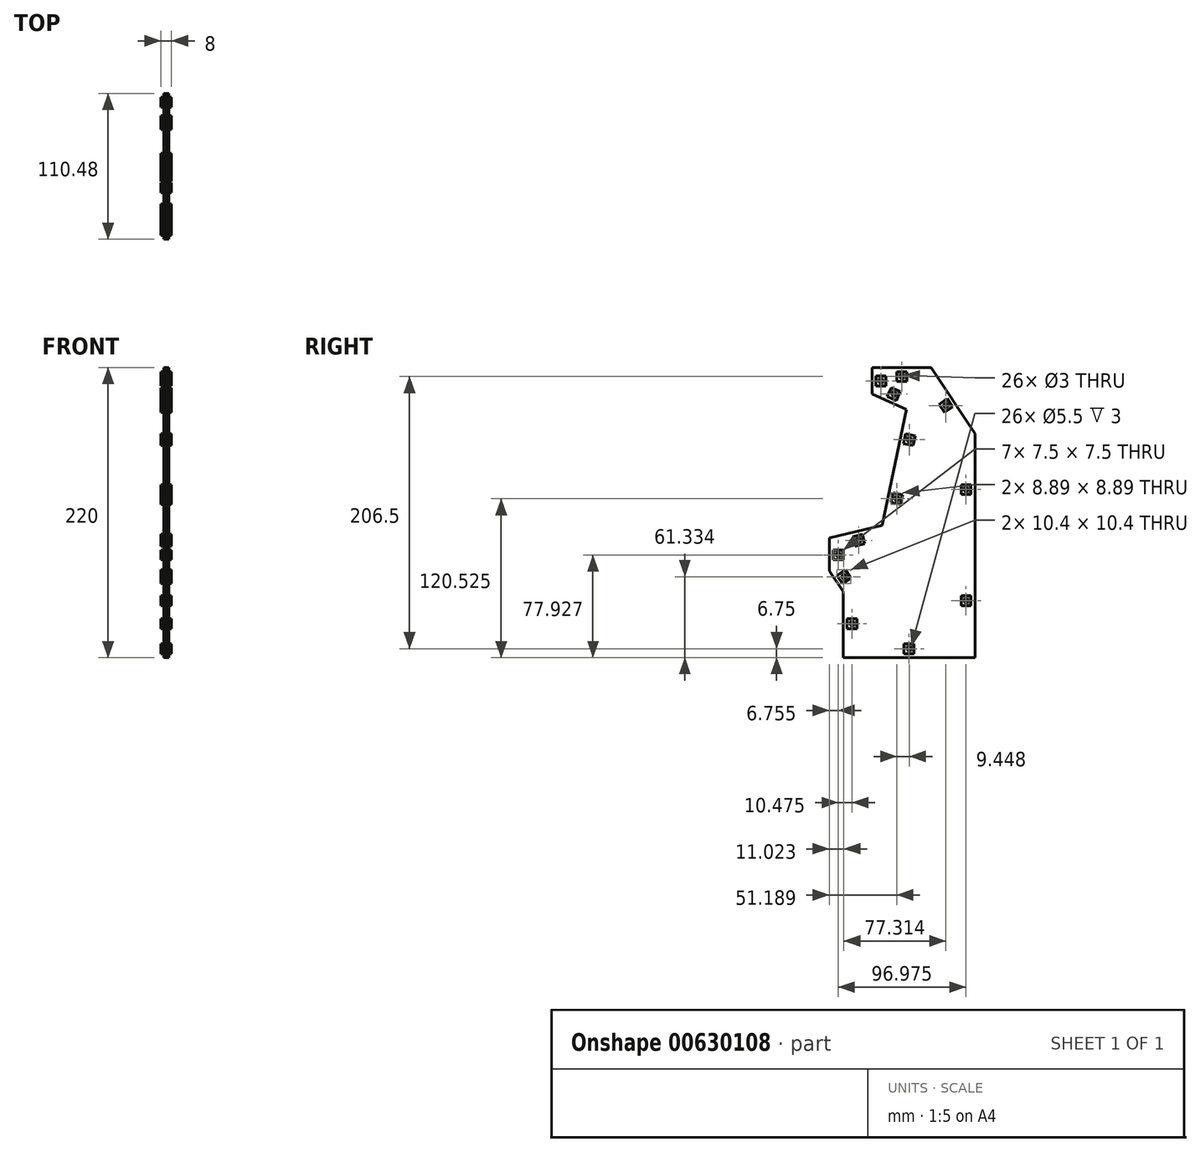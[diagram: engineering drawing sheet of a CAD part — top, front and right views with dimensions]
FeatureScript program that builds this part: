
annotation { "Feature Type Name" : "Feature", "Feature Type Description" : "" }
export const myFeature = defineFeature(function(context is Context, id is Id, definition is map)
    precondition{}
    {
        {
            var Q0;
            Q0=qCreatedBy(makeId("Right.planeOp"),FACE);
            var sketch = newSketch(context, id + "F0", { "sketchPlane" : qUnion([Q0])});
            skLineSegment(sketch, "E0", {"start": v(0, 0) * mm, "end": v(-100, 0) * mm});
            skLineSegment(sketch, "E1", {"start": v(-100, 0) * mm, "end": v(-100, 50) * mm});
            skLineSegment(sketch, "E2", {"start": v(-100, 50) * mm, "end": v(-110.48, 65.67) * mm});
            skLineSegment(sketch, "E3", {"start": v(-110.48, 65.67) * mm, "end": v(-110.48, 90.67) * mm});
            skLineSegment(sketch, "E4", {"start": v(-110.48, 90.67) * mm, "end": v(-70.49, 100.17) * mm});
            skLineSegment(sketch, "E5", {"start": v(-70.49, 100.17) * mm, "end": v(-51.9, 188.23) * mm});
            skLineSegment(sketch, "E6", {"start": v(-51.9, 188.23) * mm, "end": v(-78.17, 200) * mm});
            skLineSegment(sketch, "E7", {"start": v(-78.17, 200) * mm, "end": v(-78.17, 220) * mm});
            skLineSegment(sketch, "E8", {"start": v(-78.17, 220) * mm, "end": v(-33.17, 220) * mm});
            skLineSegment(sketch, "E9", {"start": v(-33.17, 220) * mm, "end": v(0, 170) * mm});
            skLineSegment(sketch, "E10", {"start": v(0, 170) * mm, "end": v(0, 0) * mm});
            skLineSegment(sketch, "E11.0", {"start": v(-109.48, 89.88) * mm, "end": v(-69.64, 99.35) * mm});
            skLineSegment(sketch, "E11.1", {"start": v(-109.48, 65.97) * mm, "end": v(-109.48, 89.88) * mm});
            skLineSegment(sketch, "E11.2", {"start": v(-99, 50.3) * mm, "end": v(-109.48, 65.97) * mm});
            skLineSegment(sketch, "E11.3", {"start": v(-99, 1) * mm, "end": v(-99, 50.3) * mm});
            skLineSegment(sketch, "E11.4", {"start": v(-1, 1) * mm, "end": v(-99, 1) * mm});
            skLineSegment(sketch, "E11.5", {"start": v(-69.64, 99.35) * mm, "end": v(-50.75, 188.81) * mm});
            skLineSegment(sketch, "E11.6", {"start": v(-50.75, 188.81) * mm, "end": v(-77.17, 200.65) * mm});
            skLineSegment(sketch, "E11.7", {"start": v(-77.17, 200.65) * mm, "end": v(-77.17, 219) * mm});
            skLineSegment(sketch, "E11.8", {"start": v(-77.17, 219) * mm, "end": v(-33.7, 219) * mm});
            skLineSegment(sketch, "E11.9", {"start": v(-33.7, 219) * mm, "end": v(-1, 169.7) * mm});
            skLineSegment(sketch, "E11.10", {"start": v(-1, 169.7) * mm, "end": v(-1, 1) * mm});
            skLineSegment(sketch, "E12.0", {"start": v(-75.17, 217) * mm, "end": v(-34.78, 217) * mm});
            skLineSegment(sketch, "E12.1", {"start": v(-75.17, 201.94) * mm, "end": v(-75.17, 217) * mm});
            skLineSegment(sketch, "E12.2", {"start": v(-48.46, 189.98) * mm, "end": v(-75.17, 201.94) * mm});
            skLineSegment(sketch, "E12.3", {"start": v(-67.95, 97.7) * mm, "end": v(-48.46, 189.98) * mm});
            skLineSegment(sketch, "E12.4", {"start": v(-107.48, 88.3) * mm, "end": v(-67.95, 97.7) * mm});
            skLineSegment(sketch, "E12.5", {"start": v(-34.78, 217) * mm, "end": v(-3, 169.1) * mm});
            skLineSegment(sketch, "E12.6", {"start": v(-3, 169.1) * mm, "end": v(-3, 3) * mm});
            skLineSegment(sketch, "E12.7", {"start": v(-3, 3) * mm, "end": v(-97, 3) * mm});
            skLineSegment(sketch, "E12.8", {"start": v(-97, 3) * mm, "end": v(-97, 50.91) * mm});
            skLineSegment(sketch, "E12.9", {"start": v(-97, 50.91) * mm, "end": v(-107.48, 66.58) * mm});
            skLineSegment(sketch, "E12.10", {"start": v(-107.48, 66.58) * mm, "end": v(-107.48, 88.3) * mm});
            skPoint(sketch, "E13", {"position": v(-58.2, 143.84) * mm});
            skPoint(sketch, "E14", {"position": v(-87.71, 93) * mm});
            skSolve(sketch);
        }
        {
            var Q0;
            Q0=makeQuery(id+"F0.imprint","IMPRINT",FACE,{"disambiguationData":[TD([[makeQuery(id+"F0.imprint","IMPRINT",EDGE,{"derivedFrom":sQuery(id+"F0.wireOp",EDGE,"E11.0")}),-1.0]])]});
            var Q1;
            Q1=makeQuery(id+"F0.imprint","IMPRINT",FACE,{"disambiguationData":[TD([[makeQuery(id+"F0.imprint","IMPRINT",EDGE,{"derivedFrom":sQuery(id+"F0.wireOp",EDGE,"E0")}),-1.0]])]});
            var Q2;
            Q2=makeQuery(id+"F0.imprint","IMPRINT",FACE,{"disambiguationData":[TD([[makeQuery(id+"F0.imprint","IMPRINT",EDGE,{"derivedFrom":sQuery(id+"F0.wireOp",EDGE,"E12.0")}),-1.0]])]});
            extrude(context, id + "F1", {"entities" : qUnion([Q0, Q1, Q2]), "depth" : 2 * mm, "offsetDistance" : 25 * mm});
        }
        {
            var Q0;
            Q0=makeQuery(id+"F1.opExtrude","CAP_FACE",FACE,{"disambiguationData":[OSD([sQuery(id+"F0.wireOp",EDGE,"E0"),sQuery(id+"F0.wireOp",EDGE,"E1"),sQuery(id+"F0.wireOp",EDGE,"E2"),sQuery(id+"F0.wireOp",EDGE,"E3"),sQuery(id+"F0.wireOp",EDGE,"E4"),sQuery(id+"F0.wireOp",EDGE,"E5"),sQuery(id+"F0.wireOp",EDGE,"E6"),sQuery(id+"F0.wireOp",EDGE,"E7"),sQuery(id+"F0.wireOp",EDGE,"E8"),sQuery(id+"F0.wireOp",EDGE,"E9"),sQuery(id+"F0.wireOp",EDGE,"E10")])],"isStart":true});
            var sketch = newSketch(context, id + "F2", { "sketchPlane" : qUnion([Q0])});
            skPoint(sketch, "E15", {"position": v(70.49, 100.17) * mm});
            skPoint(sketch, "E16", {"position": v(110.48, 90.67) * mm});
            skPoint(sketch, "E17", {"position": v(89.56, 94.61) * mm});
            skLineSegment(sketch, "E18", {"start": v(89.56, 94.61) * mm, "end": v(88.86, 91.7) * mm});
            skLineSegment(sketch, "E19", {"start": v(86.19, 92.33) * mm, "end": v(88.86, 91.7) * mm});
            skLineSegment(sketch, "E20", {"start": v(88.86, 91.7) * mm, "end": v(91.54, 91.06) * mm});
            skCircle(sketch, "E21", {"center": v(88.23, 89.02) * mm, "radius": 2.75 * mm});
            skLineSegment(sketch, "E22", {"start": v(88.86, 91.7) * mm, "end": v(87.6, 86.34) * mm});
            skLineSegment(sketch, "E23", {"start": v(86.19, 92.33) * mm, "end": v(84.92, 86.98) * mm});
            skLineSegment(sketch, "E24", {"start": v(91.54, 91.06) * mm, "end": v(90.27, 85.7) * mm});
            skLineSegment(sketch, "E25", {"start": v(84.92, 86.98) * mm, "end": v(90.27, 85.7) * mm});
            skLineSegment(sketch, "E26.2", {"start": v(92.74, 91.8) * mm, "end": v(91.01, 84.5) * mm});
            skLineSegment(sketch, "E26.3", {"start": v(83.71, 86.24) * mm, "end": v(91.01, 84.5) * mm});
            skLineSegment(sketch, "E26.4", {"start": v(85.45, 93.53) * mm, "end": v(83.71, 86.24) * mm});
            skCircle(sketch, "E27", {"center": v(88.23, 89.02) * mm, "radius": 1.5 * mm});
            skPoint(sketch, "E28", {"position": v(99, 25.65) * mm});
            skLineSegment(sketch, "E29", {"start": v(99, 25.65) * mm, "end": v(96, 25.65) * mm});
            skLineSegment(sketch, "E30", {"start": v(96, 28.4) * mm, "end": v(96, 25.65) * mm});
            skLineSegment(sketch, "E31", {"start": v(96, 25.65) * mm, "end": v(96, 22.9) * mm});
            skCircle(sketch, "E32", {"center": v(93.25, 25.65) * mm, "radius": 2.75 * mm});
            skLineSegment(sketch, "E33", {"start": v(96, 25.65) * mm, "end": v(90.5, 25.65) * mm});
            skLineSegment(sketch, "E34", {"start": v(96, 28.4) * mm, "end": v(90.5, 28.4) * mm});
            skLineSegment(sketch, "E35", {"start": v(96, 22.9) * mm, "end": v(90.5, 22.9) * mm});
            skLineSegment(sketch, "E36", {"start": v(90.5, 28.4) * mm, "end": v(90.5, 22.9) * mm});
            skLineSegment(sketch, "E37.2", {"start": v(97, 21.9) * mm, "end": v(89.5, 21.9) * mm});
            skLineSegment(sketch, "E37.3", {"start": v(89.5, 29.4) * mm, "end": v(89.5, 21.9) * mm});
            skLineSegment(sketch, "E37.4", {"start": v(97, 29.4) * mm, "end": v(89.5, 29.4) * mm});
            skCircle(sketch, "E38", {"center": v(93.25, 25.65) * mm, "radius": 1.5 * mm});
            skPoint(sketch, "E39", {"position": v(100, 50) * mm});
            skPoint(sketch, "E40", {"position": v(100, 0) * mm});
            skLineSegment(sketch, "E41", {"start": v(97, 21.9) * mm, "end": v(97, 29.4) * mm});
            skPoint(sketch, "E42", {"position": v(50, 0) * mm});
            skLineSegment(sketch, "E43", {"start": v(50, 1) * mm, "end": v(50, 4) * mm});
            skLineSegment(sketch, "E44", {"start": v(52.75, 4) * mm, "end": v(50, 4) * mm});
            skLineSegment(sketch, "E45", {"start": v(50, 4) * mm, "end": v(47.25, 4) * mm});
            skCircle(sketch, "E46", {"center": v(50, 6.75) * mm, "radius": 2.75 * mm});
            skLineSegment(sketch, "E47", {"start": v(50, 4) * mm, "end": v(50, 9.5) * mm});
            skLineSegment(sketch, "E48", {"start": v(52.75, 4) * mm, "end": v(52.75, 9.5) * mm});
            skLineSegment(sketch, "E49", {"start": v(47.25, 4) * mm, "end": v(47.25, 9.5) * mm});
            skLineSegment(sketch, "E50", {"start": v(52.75, 9.5) * mm, "end": v(47.25, 9.5) * mm});
            skLineSegment(sketch, "E51.2", {"start": v(46.25, 3) * mm, "end": v(46.25, 10.5) * mm});
            skLineSegment(sketch, "E51.3", {"start": v(53.75, 10.5) * mm, "end": v(46.25, 10.5) * mm});
            skLineSegment(sketch, "E51.4", {"start": v(53.75, 3) * mm, "end": v(53.75, 10.5) * mm});
            skCircle(sketch, "E52", {"center": v(50, 6.75) * mm, "radius": 1.5 * mm});
            skLineSegment(sketch, "E53", {"start": v(46.25, 3) * mm, "end": v(53.75, 3) * mm});
            skLineSegment(sketch, "E54", {"start": v(85.45, 93.53) * mm, "end": v(92.74, 91.8) * mm});
            skPoint(sketch, "E55", {"position": v(1, 43.17) * mm});
            skLineSegment(sketch, "E56", {"start": v(1, 43.17) * mm, "end": v(4, 43.17) * mm});
            skLineSegment(sketch, "E57", {"start": v(4, 40.42) * mm, "end": v(4, 43.17) * mm});
            skLineSegment(sketch, "E58", {"start": v(4, 43.17) * mm, "end": v(4, 45.92) * mm});
            skCircle(sketch, "E59", {"center": v(6.75, 43.17) * mm, "radius": 2.75 * mm});
            skLineSegment(sketch, "E60", {"start": v(4, 43.17) * mm, "end": v(9.5, 43.17) * mm});
            skLineSegment(sketch, "E61", {"start": v(4, 40.42) * mm, "end": v(9.5, 40.42) * mm});
            skLineSegment(sketch, "E62", {"start": v(4, 45.92) * mm, "end": v(9.5, 45.92) * mm});
            skLineSegment(sketch, "E63", {"start": v(9.5, 40.42) * mm, "end": v(9.5, 45.92) * mm});
            skLineSegment(sketch, "E64.2", {"start": v(3, 46.92) * mm, "end": v(10.5, 46.92) * mm});
            skLineSegment(sketch, "E64.3", {"start": v(10.5, 39.42) * mm, "end": v(10.5, 46.92) * mm});
            skLineSegment(sketch, "E64.4", {"start": v(3, 39.42) * mm, "end": v(10.5, 39.42) * mm});
            skCircle(sketch, "E65", {"center": v(6.75, 43.17) * mm, "radius": 1.5 * mm});
            skLineSegment(sketch, "E66", {"start": v(3, 46.92) * mm, "end": v(3, 39.42) * mm});
            skPoint(sketch, "E67", {"position": v(0, 170) * mm});
            skPoint(sketch, "E68", {"position": v(0, 85) * mm});
            skPoint(sketch, "E69", {"position": v(1, 127.52) * mm});
            skLineSegment(sketch, "E70", {"start": v(1, 127.52) * mm, "end": v(4, 127.52) * mm});
            skLineSegment(sketch, "E71", {"start": v(4, 124.77) * mm, "end": v(4, 127.52) * mm});
            skLineSegment(sketch, "E72", {"start": v(4, 127.52) * mm, "end": v(4, 130.27) * mm});
            skCircle(sketch, "E73", {"center": v(6.75, 127.52) * mm, "radius": 2.75 * mm});
            skLineSegment(sketch, "E74", {"start": v(4, 127.52) * mm, "end": v(9.5, 127.52) * mm});
            skLineSegment(sketch, "E75", {"start": v(4, 124.77) * mm, "end": v(9.5, 124.77) * mm});
            skLineSegment(sketch, "E76", {"start": v(4, 130.27) * mm, "end": v(9.5, 130.27) * mm});
            skLineSegment(sketch, "E77", {"start": v(9.5, 124.77) * mm, "end": v(9.5, 130.27) * mm});
            skLineSegment(sketch, "E78.2", {"start": v(3, 131.27) * mm, "end": v(10.5, 131.27) * mm});
            skLineSegment(sketch, "E78.3", {"start": v(10.5, 123.77) * mm, "end": v(10.5, 131.27) * mm});
            skLineSegment(sketch, "E78.4", {"start": v(3, 123.77) * mm, "end": v(10.5, 123.77) * mm});
            skCircle(sketch, "E79", {"center": v(6.75, 127.52) * mm, "radius": 1.5 * mm});
            skLineSegment(sketch, "E80", {"start": v(3, 131.27) * mm, "end": v(3, 123.77) * mm});
            skPoint(sketch, "E81", {"position": v(17.35, 194.35) * mm});
            skLineSegment(sketch, "E82", {"start": v(17.35, 194.35) * mm, "end": v(19.85, 192.7) * mm});
            skLineSegment(sketch, "E83", {"start": v(18.33, 190.4) * mm, "end": v(19.85, 192.7) * mm});
            skLineSegment(sketch, "E84", {"start": v(19.85, 192.7) * mm, "end": v(21.37, 194.98) * mm});
            skCircle(sketch, "E85", {"center": v(22.14, 191.17) * mm, "radius": 2.75 * mm});
            skLineSegment(sketch, "E86", {"start": v(19.85, 192.7) * mm, "end": v(24.43, 189.65) * mm});
            skLineSegment(sketch, "E87", {"start": v(18.33, 190.4) * mm, "end": v(22.91, 187.36) * mm});
            skLineSegment(sketch, "E88", {"start": v(21.37, 194.98) * mm, "end": v(25.95, 191.94) * mm});
            skLineSegment(sketch, "E89", {"start": v(22.91, 187.36) * mm, "end": v(25.95, 191.94) * mm});
            skLineSegment(sketch, "E90.2", {"start": v(21.1, 196.37) * mm, "end": v(27.34, 192.22) * mm});
            skLineSegment(sketch, "E90.3", {"start": v(23.2, 185.97) * mm, "end": v(27.34, 192.22) * mm});
            skLineSegment(sketch, "E90.4", {"start": v(16.95, 190.12) * mm, "end": v(23.2, 185.97) * mm});
            skCircle(sketch, "E91", {"center": v(22.14, 191.17) * mm, "radius": 1.5 * mm});
            skLineSegment(sketch, "E92", {"start": v(21.1, 196.37) * mm, "end": v(16.95, 190.12) * mm});
            skPoint(sketch, "E93", {"position": v(55.43, 219) * mm});
            skLineSegment(sketch, "E94", {"start": v(55.43, 219) * mm, "end": v(55.43, 216) * mm});
            skLineSegment(sketch, "E95", {"start": v(52.68, 216) * mm, "end": v(55.43, 216) * mm});
            skLineSegment(sketch, "E96", {"start": v(55.43, 216) * mm, "end": v(58.18, 216) * mm});
            skCircle(sketch, "E97", {"center": v(55.43, 213.25) * mm, "radius": 2.75 * mm});
            skLineSegment(sketch, "E98", {"start": v(55.43, 216) * mm, "end": v(55.43, 210.5) * mm});
            skLineSegment(sketch, "E99", {"start": v(52.68, 216) * mm, "end": v(52.68, 210.5) * mm});
            skLineSegment(sketch, "E100", {"start": v(58.18, 216) * mm, "end": v(58.18, 210.5) * mm});
            skLineSegment(sketch, "E101", {"start": v(52.68, 210.5) * mm, "end": v(58.18, 210.5) * mm});
            skLineSegment(sketch, "E102.2", {"start": v(59.18, 217) * mm, "end": v(59.18, 209.5) * mm});
            skLineSegment(sketch, "E102.3", {"start": v(51.68, 209.5) * mm, "end": v(59.18, 209.5) * mm});
            skLineSegment(sketch, "E102.4", {"start": v(51.68, 217) * mm, "end": v(51.68, 209.5) * mm});
            skCircle(sketch, "E103", {"center": v(55.43, 213.25) * mm, "radius": 1.5 * mm});
            skLineSegment(sketch, "E104", {"start": v(59.18, 217) * mm, "end": v(51.68, 217) * mm});
            skPoint(sketch, "E105", {"position": v(63.96, 194.73) * mm});
            skLineSegment(sketch, "E106", {"start": v(63.96, 194.73) * mm, "end": v(62.73, 197.47) * mm});
            skLineSegment(sketch, "E107", {"start": v(65.24, 198.6) * mm, "end": v(62.73, 197.47) * mm});
            skLineSegment(sketch, "E108", {"start": v(62.73, 197.47) * mm, "end": v(60.22, 196.34) * mm});
            skCircle(sketch, "E109", {"center": v(61.6, 199.98) * mm, "radius": 2.75 * mm});
            skLineSegment(sketch, "E110", {"start": v(62.73, 197.47) * mm, "end": v(60.48, 202.49) * mm});
            skLineSegment(sketch, "E111", {"start": v(65.24, 198.6) * mm, "end": v(63, 203.61) * mm});
            skLineSegment(sketch, "E112", {"start": v(60.22, 196.34) * mm, "end": v(57.97, 201.36) * mm});
            skLineSegment(sketch, "E113", {"start": v(63, 203.61) * mm, "end": v(57.97, 201.36) * mm});
            skLineSegment(sketch, "E114.2", {"start": v(59.72, 195.02) * mm, "end": v(56.65, 201.87) * mm});
            skLineSegment(sketch, "E114.3", {"start": v(63.5, 204.93) * mm, "end": v(56.65, 201.87) * mm});
            skLineSegment(sketch, "E114.4", {"start": v(66.56, 198.09) * mm, "end": v(63.5, 204.93) * mm});
            skCircle(sketch, "E115", {"center": v(61.6, 199.98) * mm, "radius": 1.5 * mm});
            skLineSegment(sketch, "E116", {"start": v(59.72, 195.02) * mm, "end": v(66.56, 198.09) * mm});
            skPoint(sketch, "E117", {"position": v(55.47, 166.45) * mm});
            skLineSegment(sketch, "E118", {"start": v(55.47, 166.45) * mm, "end": v(52.53, 165.83) * mm});
            skLineSegment(sketch, "E119", {"start": v(51.97, 168.52) * mm, "end": v(52.53, 165.83) * mm});
            skLineSegment(sketch, "E120", {"start": v(52.53, 165.83) * mm, "end": v(53.1, 163.14) * mm});
            skCircle(sketch, "E121", {"center": v(49.84, 165.26) * mm, "radius": 2.75 * mm});
            skLineSegment(sketch, "E122", {"start": v(52.53, 165.83) * mm, "end": v(47.15, 164.69) * mm});
            skLineSegment(sketch, "E123", {"start": v(51.97, 168.52) * mm, "end": v(46.58, 167.38) * mm});
            skLineSegment(sketch, "E124", {"start": v(53.1, 163.14) * mm, "end": v(47.72, 162) * mm});
            skLineSegment(sketch, "E125", {"start": v(46.58, 167.38) * mm, "end": v(47.72, 162) * mm});
            skLineSegment(sketch, "E126.2", {"start": v(54.29, 162.36) * mm, "end": v(46.95, 160.81) * mm});
            skLineSegment(sketch, "E126.3", {"start": v(45.4, 168.15) * mm, "end": v(46.95, 160.81) * mm});
            skLineSegment(sketch, "E126.4", {"start": v(52.74, 169.7) * mm, "end": v(45.4, 168.15) * mm});
            skCircle(sketch, "E127", {"center": v(49.84, 165.26) * mm, "radius": 1.5 * mm});
            skLineSegment(sketch, "E128", {"start": v(54.29, 162.36) * mm, "end": v(52.74, 169.7) * mm});
            skPoint(sketch, "E129", {"position": v(64.92, 121.71) * mm});
            skLineSegment(sketch, "E130", {"start": v(64.92, 121.71) * mm, "end": v(61.98, 121.1) * mm});
            skLineSegment(sketch, "E131", {"start": v(61.41, 123.78) * mm, "end": v(61.98, 121.1) * mm});
            skLineSegment(sketch, "E132", {"start": v(61.98, 121.1) * mm, "end": v(62.55, 118.4) * mm});
            skCircle(sketch, "E133", {"center": v(59.3, 120.52) * mm, "radius": 2.75 * mm});
            skLineSegment(sketch, "E134", {"start": v(61.98, 121.1) * mm, "end": v(56.6, 119.96) * mm});
            skLineSegment(sketch, "E135", {"start": v(61.41, 123.78) * mm, "end": v(56.03, 122.65) * mm});
            skLineSegment(sketch, "E136", {"start": v(62.55, 118.4) * mm, "end": v(57.17, 117.27) * mm});
            skLineSegment(sketch, "E137", {"start": v(56.03, 122.65) * mm, "end": v(57.17, 117.27) * mm});
            skLineSegment(sketch, "E138.2", {"start": v(63.74, 117.63) * mm, "end": v(56.4, 116.08) * mm});
            skLineSegment(sketch, "E138.3", {"start": v(54.85, 123.42) * mm, "end": v(56.4, 116.08) * mm});
            skLineSegment(sketch, "E138.4", {"start": v(62.19, 124.97) * mm, "end": v(54.85, 123.42) * mm});
            skCircle(sketch, "E139", {"center": v(59.3, 120.52) * mm, "radius": 1.5 * mm});
            skLineSegment(sketch, "E140", {"start": v(63.74, 117.63) * mm, "end": v(62.19, 124.97) * mm});
            skPoint(sketch, "E141", {"position": v(61.19, 144.2) * mm});
            skPoint(sketch, "E142", {"position": v(104.24, 58.14) * mm});
            skLineSegment(sketch, "E143", {"start": v(104.24, 58.14) * mm, "end": v(101.74, 59.8) * mm});
            skLineSegment(sketch, "E144", {"start": v(103.27, 62.1) * mm, "end": v(101.74, 59.8) * mm});
            skLineSegment(sketch, "E145", {"start": v(101.74, 59.8) * mm, "end": v(100.22, 57.52) * mm});
            skCircle(sketch, "E146", {"center": v(99.46, 61.33) * mm, "radius": 2.75 * mm});
            skLineSegment(sketch, "E147", {"start": v(101.74, 59.8) * mm, "end": v(97.17, 62.86) * mm});
            skLineSegment(sketch, "E148", {"start": v(103.27, 62.1) * mm, "end": v(98.7, 65.15) * mm});
            skLineSegment(sketch, "E149", {"start": v(100.22, 57.52) * mm, "end": v(95.64, 60.58) * mm});
            skLineSegment(sketch, "E150", {"start": v(98.7, 65.15) * mm, "end": v(95.64, 60.58) * mm});
            skLineSegment(sketch, "E151.2", {"start": v(100.5, 56.13) * mm, "end": v(94.26, 60.3) * mm});
            skLineSegment(sketch, "E151.3", {"start": v(98.42, 66.54) * mm, "end": v(94.26, 60.3) * mm});
            skLineSegment(sketch, "E151.4", {"start": v(104.66, 62.37) * mm, "end": v(98.42, 66.54) * mm});
            skCircle(sketch, "E152", {"center": v(99.46, 61.33) * mm, "radius": 1.5 * mm});
            skLineSegment(sketch, "E153", {"start": v(100.5, 56.13) * mm, "end": v(104.66, 62.37) * mm});
            skPoint(sketch, "E154", {"position": v(109.48, 77.93) * mm});
            skLineSegment(sketch, "E155", {"start": v(109.48, 77.93) * mm, "end": v(106.48, 77.93) * mm});
            skLineSegment(sketch, "E156", {"start": v(106.48, 80.68) * mm, "end": v(106.48, 77.93) * mm});
            skLineSegment(sketch, "E157", {"start": v(106.48, 77.93) * mm, "end": v(106.48, 75.18) * mm});
            skCircle(sketch, "E158", {"center": v(103.73, 77.93) * mm, "radius": 2.75 * mm});
            skLineSegment(sketch, "E159", {"start": v(106.48, 77.93) * mm, "end": v(100.98, 77.93) * mm});
            skLineSegment(sketch, "E160", {"start": v(106.48, 80.68) * mm, "end": v(100.98, 80.68) * mm});
            skLineSegment(sketch, "E161", {"start": v(106.48, 75.18) * mm, "end": v(100.98, 75.18) * mm});
            skLineSegment(sketch, "E162", {"start": v(100.98, 80.68) * mm, "end": v(100.98, 75.18) * mm});
            skLineSegment(sketch, "E163.2", {"start": v(107.48, 74.18) * mm, "end": v(99.98, 74.18) * mm});
            skLineSegment(sketch, "E163.3", {"start": v(99.98, 81.68) * mm, "end": v(99.98, 74.18) * mm});
            skLineSegment(sketch, "E163.4", {"start": v(107.48, 81.68) * mm, "end": v(99.98, 81.68) * mm});
            skCircle(sketch, "E164", {"center": v(103.73, 77.93) * mm, "radius": 1.5 * mm});
            skLineSegment(sketch, "E165", {"start": v(107.48, 74.18) * mm, "end": v(107.48, 81.68) * mm});
            skPoint(sketch, "E166", {"position": v(1, 85.35) * mm});
            skPoint(sketch, "E167", {"position": v(60.2, 144.08) * mm});
            skPoint(sketch, "E168", {"position": v(77.17, 209.82) * mm});
            skLineSegment(sketch, "E169", {"start": v(77.17, 209.82) * mm, "end": v(74.17, 209.82) * mm});
            skLineSegment(sketch, "E170", {"start": v(74.17, 212.57) * mm, "end": v(74.17, 209.82) * mm});
            skLineSegment(sketch, "E171", {"start": v(74.17, 209.82) * mm, "end": v(74.17, 207.07) * mm});
            skCircle(sketch, "E172", {"center": v(71.42, 209.82) * mm, "radius": 2.75 * mm});
            skLineSegment(sketch, "E173", {"start": v(74.17, 209.82) * mm, "end": v(68.67, 209.82) * mm});
            skLineSegment(sketch, "E174", {"start": v(74.17, 212.57) * mm, "end": v(68.67, 212.57) * mm});
            skLineSegment(sketch, "E175", {"start": v(74.17, 207.07) * mm, "end": v(68.67, 207.07) * mm});
            skLineSegment(sketch, "E176", {"start": v(68.67, 212.57) * mm, "end": v(68.67, 207.07) * mm});
            skLineSegment(sketch, "E177.2", {"start": v(75.17, 206.07) * mm, "end": v(67.67, 206.07) * mm});
            skLineSegment(sketch, "E177.3", {"start": v(67.67, 213.57) * mm, "end": v(67.67, 206.07) * mm});
            skLineSegment(sketch, "E177.4", {"start": v(75.17, 213.57) * mm, "end": v(67.67, 213.57) * mm});
            skCircle(sketch, "E178", {"center": v(71.42, 209.82) * mm, "radius": 1.5 * mm});
            skLineSegment(sketch, "E179", {"start": v(75.17, 206.07) * mm, "end": v(75.17, 213.57) * mm});
            skSolve(sketch);
        }
        {
            var Q0;
            {var subQ10=sQuery(id+"F2.wireOp",EDGE,"E19");Q0=makeQuery(id+"F2.imprint","IMPRINT",FACE,{"disambiguationData":[TD([[makeQuery(id+"F2.imprint","IMPRINT",EDGE,{"derivedFrom":subQ10}),1.0]])]});}
            var Q1;
            {var subQ10=sQuery(id+"F2.wireOp",EDGE,"E30");Q1=makeQuery(id+"F2.imprint","IMPRINT",FACE,{"disambiguationData":[TD([[makeQuery(id+"F2.imprint","IMPRINT",EDGE,{"derivedFrom":subQ10}),1.0]])]});}
            var Q2;
            {var subQ10=sQuery(id+"F2.wireOp",EDGE,"E44");Q2=makeQuery(id+"F2.imprint","IMPRINT",FACE,{"disambiguationData":[TD([[makeQuery(id+"F2.imprint","IMPRINT",EDGE,{"derivedFrom":subQ10}),1.0]])]});}
            var Q3;
            {var subQ10=sQuery(id+"F2.wireOp",EDGE,"E57");Q3=makeQuery(id+"F2.imprint","IMPRINT",FACE,{"disambiguationData":[TD([[makeQuery(id+"F2.imprint","IMPRINT",EDGE,{"derivedFrom":subQ10}),1.0]])]});}
            var Q4;
            {var subQ10=sQuery(id+"F2.wireOp",EDGE,"E71");Q4=makeQuery(id+"F2.imprint","IMPRINT",FACE,{"disambiguationData":[TD([[makeQuery(id+"F2.imprint","IMPRINT",EDGE,{"derivedFrom":subQ10}),1.0]])]});}
            var Q5;
            {var subQ10=sQuery(id+"F2.wireOp",EDGE,"E83");Q5=makeQuery(id+"F2.imprint","IMPRINT",FACE,{"disambiguationData":[TD([[makeQuery(id+"F2.imprint","IMPRINT",EDGE,{"derivedFrom":subQ10}),1.0]])]});}
            var Q6;
            {var subQ10=sQuery(id+"F2.wireOp",EDGE,"E95");Q6=makeQuery(id+"F2.imprint","IMPRINT",FACE,{"disambiguationData":[TD([[makeQuery(id+"F2.imprint","IMPRINT",EDGE,{"derivedFrom":subQ10}),1.0]])]});}
            var Q7;
            {var subQ10=sQuery(id+"F2.wireOp",EDGE,"E107");Q7=makeQuery(id+"F2.imprint","IMPRINT",FACE,{"disambiguationData":[TD([[makeQuery(id+"F2.imprint","IMPRINT",EDGE,{"derivedFrom":subQ10}),1.0]])]});}
            var Q8;
            {var subQ10=sQuery(id+"F2.wireOp",EDGE,"E119");Q8=makeQuery(id+"F2.imprint","IMPRINT",FACE,{"disambiguationData":[TD([[makeQuery(id+"F2.imprint","IMPRINT",EDGE,{"derivedFrom":subQ10}),1.0]])]});}
            var Q9;
            {var subQ10=sQuery(id+"F2.wireOp",EDGE,"E131");Q9=makeQuery(id+"F2.imprint","IMPRINT",FACE,{"disambiguationData":[TD([[makeQuery(id+"F2.imprint","IMPRINT",EDGE,{"derivedFrom":subQ10}),1.0]])]});}
            var Q10;
            {var subQ10=sQuery(id+"F2.wireOp",EDGE,"E144");Q10=makeQuery(id+"F2.imprint","IMPRINT",FACE,{"disambiguationData":[TD([[makeQuery(id+"F2.imprint","IMPRINT",EDGE,{"derivedFrom":subQ10}),1.0]])]});}
            var Q11;
            {var subQ10=sQuery(id+"F2.wireOp",EDGE,"E156");Q11=makeQuery(id+"F2.imprint","IMPRINT",FACE,{"disambiguationData":[TD([[makeQuery(id+"F2.imprint","IMPRINT",EDGE,{"derivedFrom":subQ10}),1.0]])]});}
            var Q12;
            {var subQ0=sQuery(id+"F2.wireOp",EDGE,"E19");Q12=makeQuery(id+"F2.imprint","IMPRINT",FACE,{"disambiguationData":[TD([[makeQuery(id+"F2.imprint","IMPRINT",EDGE,{"derivedFrom":subQ0}),-1.0]])]});}
            var Q13;
            {var subQ0=sQuery(id+"F2.wireOp",EDGE,"E25");var subQ3=sQuery(id+"F2.wireOp",EDGE,"E23");var subQ5=makeQuery(id+"F2.imprint","INTERSECT",VERTEX,{"derivedFrom":[subQ3,subQ0]});Q13=makeQuery(id+"F2.imprint","IMPRINT",FACE,{"disambiguationData":[TD([[makeQuery(id+"F2.imprint","IMPRINT",EDGE,{"disambiguationData":[TD([[subQ5,1.0]])],"derivedFrom":subQ3}),1.0]])]});}
            var Q14;
            {var subQ0=sQuery(id+"F2.wireOp",EDGE,"E25");var subQ3=sQuery(id+"F2.wireOp",EDGE,"E24");var subQ5=makeQuery(id+"F2.imprint","INTERSECT",VERTEX,{"derivedFrom":[subQ3,subQ0]});Q14=makeQuery(id+"F2.imprint","IMPRINT",FACE,{"disambiguationData":[TD([[makeQuery(id+"F2.imprint","IMPRINT",EDGE,{"disambiguationData":[TD([[subQ5,1.0]])],"derivedFrom":subQ3}),-1.0]])]});}
            var Q15;
            {var subQ0=sQuery(id+"F2.wireOp",EDGE,"E20");Q15=makeQuery(id+"F2.imprint","IMPRINT",FACE,{"disambiguationData":[TD([[makeQuery(id+"F2.imprint","IMPRINT",EDGE,{"derivedFrom":subQ0}),-1.0]])]});}
            var Q16;
            {var subQ0=sQuery(id+"F2.wireOp",EDGE,"E22");var subQ3=sQuery(id+"F2.wireOp",EDGE,"E27");var subQ5=makeQuery(id+"F2.imprint","INTERSECT",VERTEX,{"disambiguationData":[OD(0.0)],"derivedFrom":[subQ0,subQ3]});Q16=makeQuery(id+"F2.imprint","IMPRINT",FACE,{"disambiguationData":[TD([[makeQuery(id+"F2.imprint","IMPRINT",EDGE,{"disambiguationData":[TD([[subQ5,1.0]])],"derivedFrom":subQ3}),-1.0]])]});}
            var Q17;
            {var subQ0=sQuery(id+"F2.wireOp",EDGE,"E22");var subQ3=sQuery(id+"F2.wireOp",EDGE,"E27");var subQ4=makeQuery(id+"F2.imprint","INTERSECT",VERTEX,{"disambiguationData":[OD(0.0)],"derivedFrom":[subQ0,subQ3]});Q17=makeQuery(id+"F2.imprint","IMPRINT",FACE,{"disambiguationData":[TD([[makeQuery(id+"F2.imprint","IMPRINT",EDGE,{"disambiguationData":[TD([[subQ4,-1.0]])],"derivedFrom":subQ3}),-1.0]])]});}
            var Q18;
            {var subQ0=sQuery(id+"F2.wireOp",EDGE,"E30");Q18=makeQuery(id+"F2.imprint","IMPRINT",FACE,{"disambiguationData":[TD([[makeQuery(id+"F2.imprint","IMPRINT",EDGE,{"derivedFrom":subQ0}),-1.0]])]});}
            var Q19;
            {var subQ0=sQuery(id+"F2.wireOp",EDGE,"E36");var subQ3=sQuery(id+"F2.wireOp",EDGE,"E34");var subQ5=makeQuery(id+"F2.imprint","INTERSECT",VERTEX,{"derivedFrom":[subQ3,subQ0]});Q19=makeQuery(id+"F2.imprint","IMPRINT",FACE,{"disambiguationData":[TD([[makeQuery(id+"F2.imprint","IMPRINT",EDGE,{"disambiguationData":[TD([[subQ5,1.0]])],"derivedFrom":subQ3}),1.0]])]});}
            var Q20;
            {var subQ0=sQuery(id+"F2.wireOp",EDGE,"E36");var subQ3=sQuery(id+"F2.wireOp",EDGE,"E35");var subQ5=makeQuery(id+"F2.imprint","INTERSECT",VERTEX,{"derivedFrom":[subQ3,subQ0]});Q20=makeQuery(id+"F2.imprint","IMPRINT",FACE,{"disambiguationData":[TD([[makeQuery(id+"F2.imprint","IMPRINT",EDGE,{"disambiguationData":[TD([[subQ5,1.0]])],"derivedFrom":subQ3}),-1.0]])]});}
            var Q21;
            {var subQ0=sQuery(id+"F2.wireOp",EDGE,"E31");Q21=makeQuery(id+"F2.imprint","IMPRINT",FACE,{"disambiguationData":[TD([[makeQuery(id+"F2.imprint","IMPRINT",EDGE,{"derivedFrom":subQ0}),-1.0]])]});}
            var Q22;
            {var subQ0=sQuery(id+"F2.wireOp",EDGE,"E33");var subQ3=sQuery(id+"F2.wireOp",EDGE,"E38");var subQ4=makeQuery(id+"F2.imprint","INTERSECT",VERTEX,{"disambiguationData":[OD(0.0)],"derivedFrom":[subQ0,subQ3]});Q22=makeQuery(id+"F2.imprint","IMPRINT",FACE,{"disambiguationData":[TD([[makeQuery(id+"F2.imprint","IMPRINT",EDGE,{"disambiguationData":[TD([[subQ4,-1.0]])],"derivedFrom":subQ3}),-1.0]])]});}
            var Q23;
            {var subQ0=sQuery(id+"F2.wireOp",EDGE,"E33");var subQ3=sQuery(id+"F2.wireOp",EDGE,"E38");var subQ5=makeQuery(id+"F2.imprint","INTERSECT",VERTEX,{"disambiguationData":[OD(0.0)],"derivedFrom":[subQ0,subQ3]});Q23=makeQuery(id+"F2.imprint","IMPRINT",FACE,{"disambiguationData":[TD([[makeQuery(id+"F2.imprint","IMPRINT",EDGE,{"disambiguationData":[TD([[subQ5,1.0]])],"derivedFrom":subQ3}),-1.0]])]});}
            var Q24;
            {var subQ0=sQuery(id+"F2.wireOp",EDGE,"E50");var subQ3=sQuery(id+"F2.wireOp",EDGE,"E48");var subQ5=makeQuery(id+"F2.imprint","INTERSECT",VERTEX,{"derivedFrom":[subQ3,subQ0]});Q24=makeQuery(id+"F2.imprint","IMPRINT",FACE,{"disambiguationData":[TD([[makeQuery(id+"F2.imprint","IMPRINT",EDGE,{"disambiguationData":[TD([[subQ5,1.0]])],"derivedFrom":subQ3}),1.0]])]});}
            var Q25;
            {var subQ0=sQuery(id+"F2.wireOp",EDGE,"E50");var subQ3=sQuery(id+"F2.wireOp",EDGE,"E49");var subQ5=makeQuery(id+"F2.imprint","INTERSECT",VERTEX,{"derivedFrom":[subQ3,subQ0]});Q25=makeQuery(id+"F2.imprint","IMPRINT",FACE,{"disambiguationData":[TD([[makeQuery(id+"F2.imprint","IMPRINT",EDGE,{"disambiguationData":[TD([[subQ5,1.0]])],"derivedFrom":subQ3}),-1.0]])]});}
            var Q26;
            {var subQ0=sQuery(id+"F2.wireOp",EDGE,"E47");var subQ3=sQuery(id+"F2.wireOp",EDGE,"E52");var subQ6=makeQuery(id+"F2.imprint","INTERSECT",VERTEX,{"disambiguationData":[OD(0.0)],"derivedFrom":[subQ0,subQ3]});Q26=makeQuery(id+"F2.imprint","IMPRINT",FACE,{"disambiguationData":[TD([[makeQuery(id+"F2.imprint","IMPRINT",EDGE,{"disambiguationData":[TD([[subQ6,1.0]])],"derivedFrom":subQ3}),-1.0]])]});}
            var Q27;
            {var subQ0=sQuery(id+"F2.wireOp",EDGE,"E45");Q27=makeQuery(id+"F2.imprint","IMPRINT",FACE,{"disambiguationData":[TD([[makeQuery(id+"F2.imprint","IMPRINT",EDGE,{"derivedFrom":subQ0}),-1.0]])]});}
            var Q28;
            {var subQ0=sQuery(id+"F2.wireOp",EDGE,"E47");var subQ3=sQuery(id+"F2.wireOp",EDGE,"E52");var subQ4=makeQuery(id+"F2.imprint","INTERSECT",VERTEX,{"disambiguationData":[OD(0.0)],"derivedFrom":[subQ0,subQ3]});Q28=makeQuery(id+"F2.imprint","IMPRINT",FACE,{"disambiguationData":[TD([[makeQuery(id+"F2.imprint","IMPRINT",EDGE,{"disambiguationData":[TD([[subQ4,-1.0]])],"derivedFrom":subQ3}),-1.0]])]});}
            var Q29;
            {var subQ0=sQuery(id+"F2.wireOp",EDGE,"E44");Q29=makeQuery(id+"F2.imprint","IMPRINT",FACE,{"disambiguationData":[TD([[makeQuery(id+"F2.imprint","IMPRINT",EDGE,{"derivedFrom":subQ0}),-1.0]])]});}
            var Q30;
            {var subQ0=sQuery(id+"F2.wireOp",EDGE,"E58");Q30=makeQuery(id+"F2.imprint","IMPRINT",FACE,{"disambiguationData":[TD([[makeQuery(id+"F2.imprint","IMPRINT",EDGE,{"derivedFrom":subQ0}),-1.0]])]});}
            var Q31;
            {var subQ0=sQuery(id+"F2.wireOp",EDGE,"E63");var subQ3=sQuery(id+"F2.wireOp",EDGE,"E62");var subQ5=makeQuery(id+"F2.imprint","INTERSECT",VERTEX,{"derivedFrom":[subQ3,subQ0]});Q31=makeQuery(id+"F2.imprint","IMPRINT",FACE,{"disambiguationData":[TD([[makeQuery(id+"F2.imprint","IMPRINT",EDGE,{"disambiguationData":[TD([[subQ5,1.0]])],"derivedFrom":subQ3}),-1.0]])]});}
            var Q32;
            {var subQ0=sQuery(id+"F2.wireOp",EDGE,"E60");var subQ3=sQuery(id+"F2.wireOp",EDGE,"E65");var subQ4=makeQuery(id+"F2.imprint","INTERSECT",VERTEX,{"disambiguationData":[OD(0.0)],"derivedFrom":[subQ0,subQ3]});Q32=makeQuery(id+"F2.imprint","IMPRINT",FACE,{"disambiguationData":[TD([[makeQuery(id+"F2.imprint","IMPRINT",EDGE,{"disambiguationData":[TD([[subQ4,-1.0]])],"derivedFrom":subQ3}),-1.0]])]});}
            var Q33;
            {var subQ0=sQuery(id+"F2.wireOp",EDGE,"E60");var subQ3=sQuery(id+"F2.wireOp",EDGE,"E65");var subQ6=makeQuery(id+"F2.imprint","INTERSECT",VERTEX,{"disambiguationData":[OD(0.0)],"derivedFrom":[subQ0,subQ3]});Q33=makeQuery(id+"F2.imprint","IMPRINT",FACE,{"disambiguationData":[TD([[makeQuery(id+"F2.imprint","IMPRINT",EDGE,{"disambiguationData":[TD([[subQ6,1.0]])],"derivedFrom":subQ3}),-1.0]])]});}
            var Q34;
            {var subQ0=sQuery(id+"F2.wireOp",EDGE,"E57");Q34=makeQuery(id+"F2.imprint","IMPRINT",FACE,{"disambiguationData":[TD([[makeQuery(id+"F2.imprint","IMPRINT",EDGE,{"derivedFrom":subQ0}),-1.0]])]});}
            var Q35;
            {var subQ0=sQuery(id+"F2.wireOp",EDGE,"E63");var subQ3=sQuery(id+"F2.wireOp",EDGE,"E61");var subQ5=makeQuery(id+"F2.imprint","INTERSECT",VERTEX,{"derivedFrom":[subQ3,subQ0]});Q35=makeQuery(id+"F2.imprint","IMPRINT",FACE,{"disambiguationData":[TD([[makeQuery(id+"F2.imprint","IMPRINT",EDGE,{"disambiguationData":[TD([[subQ5,1.0]])],"derivedFrom":subQ3}),1.0]])]});}
            var Q36;
            {var subQ0=sQuery(id+"F2.wireOp",EDGE,"E72");Q36=makeQuery(id+"F2.imprint","IMPRINT",FACE,{"disambiguationData":[TD([[makeQuery(id+"F2.imprint","IMPRINT",EDGE,{"derivedFrom":subQ0}),-1.0]])]});}
            var Q37;
            {var subQ0=sQuery(id+"F2.wireOp",EDGE,"E74");var subQ3=sQuery(id+"F2.wireOp",EDGE,"E79");var subQ6=makeQuery(id+"F2.imprint","INTERSECT",VERTEX,{"disambiguationData":[OD(0.0)],"derivedFrom":[subQ0,subQ3]});Q37=makeQuery(id+"F2.imprint","IMPRINT",FACE,{"disambiguationData":[TD([[makeQuery(id+"F2.imprint","IMPRINT",EDGE,{"disambiguationData":[TD([[subQ6,1.0]])],"derivedFrom":subQ3}),-1.0]])]});}
            var Q38;
            {var subQ0=sQuery(id+"F2.wireOp",EDGE,"E74");var subQ3=sQuery(id+"F2.wireOp",EDGE,"E79");var subQ4=makeQuery(id+"F2.imprint","INTERSECT",VERTEX,{"disambiguationData":[OD(0.0)],"derivedFrom":[subQ0,subQ3]});Q38=makeQuery(id+"F2.imprint","IMPRINT",FACE,{"disambiguationData":[TD([[makeQuery(id+"F2.imprint","IMPRINT",EDGE,{"disambiguationData":[TD([[subQ4,-1.0]])],"derivedFrom":subQ3}),-1.0]])]});}
            var Q39;
            {var subQ0=sQuery(id+"F2.wireOp",EDGE,"E71");Q39=makeQuery(id+"F2.imprint","IMPRINT",FACE,{"disambiguationData":[TD([[makeQuery(id+"F2.imprint","IMPRINT",EDGE,{"derivedFrom":subQ0}),-1.0]])]});}
            var Q40;
            {var subQ0=sQuery(id+"F2.wireOp",EDGE,"E77");var subQ3=sQuery(id+"F2.wireOp",EDGE,"E75");var subQ5=makeQuery(id+"F2.imprint","INTERSECT",VERTEX,{"derivedFrom":[subQ3,subQ0]});Q40=makeQuery(id+"F2.imprint","IMPRINT",FACE,{"disambiguationData":[TD([[makeQuery(id+"F2.imprint","IMPRINT",EDGE,{"disambiguationData":[TD([[subQ5,1.0]])],"derivedFrom":subQ3}),1.0]])]});}
            var Q41;
            {var subQ0=sQuery(id+"F2.wireOp",EDGE,"E77");var subQ3=sQuery(id+"F2.wireOp",EDGE,"E76");var subQ5=makeQuery(id+"F2.imprint","INTERSECT",VERTEX,{"derivedFrom":[subQ3,subQ0]});Q41=makeQuery(id+"F2.imprint","IMPRINT",FACE,{"disambiguationData":[TD([[makeQuery(id+"F2.imprint","IMPRINT",EDGE,{"disambiguationData":[TD([[subQ5,1.0]])],"derivedFrom":subQ3}),-1.0]])]});}
            var Q42;
            {var subQ0=sQuery(id+"F2.wireOp",EDGE,"E84");Q42=makeQuery(id+"F2.imprint","IMPRINT",FACE,{"disambiguationData":[TD([[makeQuery(id+"F2.imprint","IMPRINT",EDGE,{"derivedFrom":subQ0}),-1.0]])]});}
            var Q43;
            {var subQ0=sQuery(id+"F2.wireOp",EDGE,"E86");var subQ3=sQuery(id+"F2.wireOp",EDGE,"E91");var subQ6=makeQuery(id+"F2.imprint","INTERSECT",VERTEX,{"disambiguationData":[OD(0.0)],"derivedFrom":[subQ0,subQ3]});Q43=makeQuery(id+"F2.imprint","IMPRINT",FACE,{"disambiguationData":[TD([[makeQuery(id+"F2.imprint","IMPRINT",EDGE,{"disambiguationData":[TD([[subQ6,1.0]])],"derivedFrom":subQ3}),-1.0]])]});}
            var Q44;
            {var subQ0=sQuery(id+"F2.wireOp",EDGE,"E83");Q44=makeQuery(id+"F2.imprint","IMPRINT",FACE,{"disambiguationData":[TD([[makeQuery(id+"F2.imprint","IMPRINT",EDGE,{"derivedFrom":subQ0}),-1.0]])]});}
            var Q45;
            {var subQ0=sQuery(id+"F2.wireOp",EDGE,"E86");var subQ3=sQuery(id+"F2.wireOp",EDGE,"E91");var subQ4=makeQuery(id+"F2.imprint","INTERSECT",VERTEX,{"disambiguationData":[OD(0.0)],"derivedFrom":[subQ0,subQ3]});Q45=makeQuery(id+"F2.imprint","IMPRINT",FACE,{"disambiguationData":[TD([[makeQuery(id+"F2.imprint","IMPRINT",EDGE,{"disambiguationData":[TD([[subQ4,-1.0]])],"derivedFrom":subQ3}),-1.0]])]});}
            var Q46;
            {var subQ0=sQuery(id+"F2.wireOp",EDGE,"E89");var subQ3=sQuery(id+"F2.wireOp",EDGE,"E88");var subQ5=makeQuery(id+"F2.imprint","INTERSECT",VERTEX,{"derivedFrom":[subQ3,subQ0]});Q46=makeQuery(id+"F2.imprint","IMPRINT",FACE,{"disambiguationData":[TD([[makeQuery(id+"F2.imprint","IMPRINT",EDGE,{"disambiguationData":[TD([[subQ5,1.0]])],"derivedFrom":subQ3}),-1.0]])]});}
            var Q47;
            {var subQ0=sQuery(id+"F2.wireOp",EDGE,"E89");var subQ3=sQuery(id+"F2.wireOp",EDGE,"E87");var subQ5=makeQuery(id+"F2.imprint","INTERSECT",VERTEX,{"derivedFrom":[subQ3,subQ0]});Q47=makeQuery(id+"F2.imprint","IMPRINT",FACE,{"disambiguationData":[TD([[makeQuery(id+"F2.imprint","IMPRINT",EDGE,{"disambiguationData":[TD([[subQ5,1.0]])],"derivedFrom":subQ3}),1.0]])]});}
            var Q48;
            {var subQ0=sQuery(id+"F2.wireOp",EDGE,"E95");Q48=makeQuery(id+"F2.imprint","IMPRINT",FACE,{"disambiguationData":[TD([[makeQuery(id+"F2.imprint","IMPRINT",EDGE,{"derivedFrom":subQ0}),-1.0]])]});}
            var Q49;
            {var subQ0=sQuery(id+"F2.wireOp",EDGE,"E98");var subQ3=sQuery(id+"F2.wireOp",EDGE,"E103");var subQ4=makeQuery(id+"F2.imprint","INTERSECT",VERTEX,{"disambiguationData":[OD(0.0)],"derivedFrom":[subQ0,subQ3]});Q49=makeQuery(id+"F2.imprint","IMPRINT",FACE,{"disambiguationData":[TD([[makeQuery(id+"F2.imprint","IMPRINT",EDGE,{"disambiguationData":[TD([[subQ4,-1.0]])],"derivedFrom":subQ3}),-1.0]])]});}
            var Q50;
            {var subQ0=sQuery(id+"F2.wireOp",EDGE,"E98");var subQ3=sQuery(id+"F2.wireOp",EDGE,"E103");var subQ6=makeQuery(id+"F2.imprint","INTERSECT",VERTEX,{"disambiguationData":[OD(0.0)],"derivedFrom":[subQ0,subQ3]});Q50=makeQuery(id+"F2.imprint","IMPRINT",FACE,{"disambiguationData":[TD([[makeQuery(id+"F2.imprint","IMPRINT",EDGE,{"disambiguationData":[TD([[subQ6,1.0]])],"derivedFrom":subQ3}),-1.0]])]});}
            var Q51;
            {var subQ0=sQuery(id+"F2.wireOp",EDGE,"E96");Q51=makeQuery(id+"F2.imprint","IMPRINT",FACE,{"disambiguationData":[TD([[makeQuery(id+"F2.imprint","IMPRINT",EDGE,{"derivedFrom":subQ0}),-1.0]])]});}
            var Q52;
            {var subQ0=sQuery(id+"F2.wireOp",EDGE,"E101");var subQ3=sQuery(id+"F2.wireOp",EDGE,"E100");var subQ5=makeQuery(id+"F2.imprint","INTERSECT",VERTEX,{"derivedFrom":[subQ3,subQ0]});Q52=makeQuery(id+"F2.imprint","IMPRINT",FACE,{"disambiguationData":[TD([[makeQuery(id+"F2.imprint","IMPRINT",EDGE,{"disambiguationData":[TD([[subQ5,1.0]])],"derivedFrom":subQ3}),-1.0]])]});}
            var Q53;
            {var subQ0=sQuery(id+"F2.wireOp",EDGE,"E101");var subQ3=sQuery(id+"F2.wireOp",EDGE,"E99");var subQ5=makeQuery(id+"F2.imprint","INTERSECT",VERTEX,{"derivedFrom":[subQ3,subQ0]});Q53=makeQuery(id+"F2.imprint","IMPRINT",FACE,{"disambiguationData":[TD([[makeQuery(id+"F2.imprint","IMPRINT",EDGE,{"disambiguationData":[TD([[subQ5,1.0]])],"derivedFrom":subQ3}),1.0]])]});}
            var Q54;
            {var subQ0=sQuery(id+"F2.wireOp",EDGE,"E113");var subQ3=sQuery(id+"F2.wireOp",EDGE,"E111");var subQ5=makeQuery(id+"F2.imprint","INTERSECT",VERTEX,{"derivedFrom":[subQ3,subQ0]});Q54=makeQuery(id+"F2.imprint","IMPRINT",FACE,{"disambiguationData":[TD([[makeQuery(id+"F2.imprint","IMPRINT",EDGE,{"disambiguationData":[TD([[subQ5,1.0]])],"derivedFrom":subQ3}),1.0]])]});}
            var Q55;
            {var subQ0=sQuery(id+"F2.wireOp",EDGE,"E113");var subQ3=sQuery(id+"F2.wireOp",EDGE,"E112");var subQ5=makeQuery(id+"F2.imprint","INTERSECT",VERTEX,{"derivedFrom":[subQ3,subQ0]});Q55=makeQuery(id+"F2.imprint","IMPRINT",FACE,{"disambiguationData":[TD([[makeQuery(id+"F2.imprint","IMPRINT",EDGE,{"disambiguationData":[TD([[subQ5,1.0]])],"derivedFrom":subQ3}),-1.0]])]});}
            var Q56;
            {var subQ0=sQuery(id+"F2.wireOp",EDGE,"E110");var subQ3=sQuery(id+"F2.wireOp",EDGE,"E115");var subQ6=makeQuery(id+"F2.imprint","INTERSECT",VERTEX,{"disambiguationData":[OD(0.0)],"derivedFrom":[subQ0,subQ3]});Q56=makeQuery(id+"F2.imprint","IMPRINT",FACE,{"disambiguationData":[TD([[makeQuery(id+"F2.imprint","IMPRINT",EDGE,{"disambiguationData":[TD([[subQ6,1.0]])],"derivedFrom":subQ3}),-1.0]])]});}
            var Q57;
            {var subQ0=sQuery(id+"F2.wireOp",EDGE,"E110");var subQ3=sQuery(id+"F2.wireOp",EDGE,"E115");var subQ4=makeQuery(id+"F2.imprint","INTERSECT",VERTEX,{"disambiguationData":[OD(0.0)],"derivedFrom":[subQ0,subQ3]});Q57=makeQuery(id+"F2.imprint","IMPRINT",FACE,{"disambiguationData":[TD([[makeQuery(id+"F2.imprint","IMPRINT",EDGE,{"disambiguationData":[TD([[subQ4,-1.0]])],"derivedFrom":subQ3}),-1.0]])]});}
            var Q58;
            {var subQ0=sQuery(id+"F2.wireOp",EDGE,"E107");Q58=makeQuery(id+"F2.imprint","IMPRINT",FACE,{"disambiguationData":[TD([[makeQuery(id+"F2.imprint","IMPRINT",EDGE,{"derivedFrom":subQ0}),-1.0]])]});}
            var Q59;
            {var subQ0=sQuery(id+"F2.wireOp",EDGE,"E108");Q59=makeQuery(id+"F2.imprint","IMPRINT",FACE,{"disambiguationData":[TD([[makeQuery(id+"F2.imprint","IMPRINT",EDGE,{"derivedFrom":subQ0}),-1.0]])]});}
            var Q60;
            {var subQ0=sQuery(id+"F2.wireOp",EDGE,"E125");var subQ3=sQuery(id+"F2.wireOp",EDGE,"E123");var subQ5=makeQuery(id+"F2.imprint","INTERSECT",VERTEX,{"derivedFrom":[subQ3,subQ0]});Q60=makeQuery(id+"F2.imprint","IMPRINT",FACE,{"disambiguationData":[TD([[makeQuery(id+"F2.imprint","IMPRINT",EDGE,{"disambiguationData":[TD([[subQ5,1.0]])],"derivedFrom":subQ3}),1.0]])]});}
            var Q61;
            {var subQ0=sQuery(id+"F2.wireOp",EDGE,"E122");var subQ3=sQuery(id+"F2.wireOp",EDGE,"E127");var subQ4=makeQuery(id+"F2.imprint","INTERSECT",VERTEX,{"disambiguationData":[OD(0.0)],"derivedFrom":[subQ0,subQ3]});Q61=makeQuery(id+"F2.imprint","IMPRINT",FACE,{"disambiguationData":[TD([[makeQuery(id+"F2.imprint","IMPRINT",EDGE,{"disambiguationData":[TD([[subQ4,-1.0]])],"derivedFrom":subQ3}),-1.0]])]});}
            var Q62;
            {var subQ0=sQuery(id+"F2.wireOp",EDGE,"E119");Q62=makeQuery(id+"F2.imprint","IMPRINT",FACE,{"disambiguationData":[TD([[makeQuery(id+"F2.imprint","IMPRINT",EDGE,{"derivedFrom":subQ0}),-1.0]])]});}
            var Q63;
            {var subQ0=sQuery(id+"F2.wireOp",EDGE,"E122");var subQ3=sQuery(id+"F2.wireOp",EDGE,"E127");var subQ6=makeQuery(id+"F2.imprint","INTERSECT",VERTEX,{"disambiguationData":[OD(0.0)],"derivedFrom":[subQ0,subQ3]});Q63=makeQuery(id+"F2.imprint","IMPRINT",FACE,{"disambiguationData":[TD([[makeQuery(id+"F2.imprint","IMPRINT",EDGE,{"disambiguationData":[TD([[subQ6,1.0]])],"derivedFrom":subQ3}),-1.0]])]});}
            var Q64;
            {var subQ0=sQuery(id+"F2.wireOp",EDGE,"E120");Q64=makeQuery(id+"F2.imprint","IMPRINT",FACE,{"disambiguationData":[TD([[makeQuery(id+"F2.imprint","IMPRINT",EDGE,{"derivedFrom":subQ0}),-1.0]])]});}
            var Q65;
            {var subQ0=sQuery(id+"F2.wireOp",EDGE,"E125");var subQ3=sQuery(id+"F2.wireOp",EDGE,"E124");var subQ5=makeQuery(id+"F2.imprint","INTERSECT",VERTEX,{"derivedFrom":[subQ3,subQ0]});Q65=makeQuery(id+"F2.imprint","IMPRINT",FACE,{"disambiguationData":[TD([[makeQuery(id+"F2.imprint","IMPRINT",EDGE,{"disambiguationData":[TD([[subQ5,1.0]])],"derivedFrom":subQ3}),-1.0]])]});}
            var Q66;
            {var subQ0=sQuery(id+"F2.wireOp",EDGE,"E137");var subQ3=sQuery(id+"F2.wireOp",EDGE,"E135");var subQ5=makeQuery(id+"F2.imprint","INTERSECT",VERTEX,{"derivedFrom":[subQ3,subQ0]});Q66=makeQuery(id+"F2.imprint","IMPRINT",FACE,{"disambiguationData":[TD([[makeQuery(id+"F2.imprint","IMPRINT",EDGE,{"disambiguationData":[TD([[subQ5,1.0]])],"derivedFrom":subQ3}),1.0]])]});}
            var Q67;
            {var subQ0=sQuery(id+"F2.wireOp",EDGE,"E134");var subQ3=sQuery(id+"F2.wireOp",EDGE,"E139");var subQ4=makeQuery(id+"F2.imprint","INTERSECT",VERTEX,{"disambiguationData":[OD(0.0)],"derivedFrom":[subQ0,subQ3]});Q67=makeQuery(id+"F2.imprint","IMPRINT",FACE,{"disambiguationData":[TD([[makeQuery(id+"F2.imprint","IMPRINT",EDGE,{"disambiguationData":[TD([[subQ4,-1.0]])],"derivedFrom":subQ3}),-1.0]])]});}
            var Q68;
            {var subQ0=sQuery(id+"F2.wireOp",EDGE,"E131");Q68=makeQuery(id+"F2.imprint","IMPRINT",FACE,{"disambiguationData":[TD([[makeQuery(id+"F2.imprint","IMPRINT",EDGE,{"derivedFrom":subQ0}),-1.0]])]});}
            var Q69;
            {var subQ0=sQuery(id+"F2.wireOp",EDGE,"E134");var subQ3=sQuery(id+"F2.wireOp",EDGE,"E139");var subQ6=makeQuery(id+"F2.imprint","INTERSECT",VERTEX,{"disambiguationData":[OD(0.0)],"derivedFrom":[subQ0,subQ3]});Q69=makeQuery(id+"F2.imprint","IMPRINT",FACE,{"disambiguationData":[TD([[makeQuery(id+"F2.imprint","IMPRINT",EDGE,{"disambiguationData":[TD([[subQ6,1.0]])],"derivedFrom":subQ3}),-1.0]])]});}
            var Q70;
            {var subQ0=sQuery(id+"F2.wireOp",EDGE,"E132");Q70=makeQuery(id+"F2.imprint","IMPRINT",FACE,{"disambiguationData":[TD([[makeQuery(id+"F2.imprint","IMPRINT",EDGE,{"derivedFrom":subQ0}),-1.0]])]});}
            var Q71;
            {var subQ0=sQuery(id+"F2.wireOp",EDGE,"E137");var subQ3=sQuery(id+"F2.wireOp",EDGE,"E136");var subQ5=makeQuery(id+"F2.imprint","INTERSECT",VERTEX,{"derivedFrom":[subQ3,subQ0]});Q71=makeQuery(id+"F2.imprint","IMPRINT",FACE,{"disambiguationData":[TD([[makeQuery(id+"F2.imprint","IMPRINT",EDGE,{"disambiguationData":[TD([[subQ5,1.0]])],"derivedFrom":subQ3}),-1.0]])]});}
            var Q72;
            {var subQ0=sQuery(id+"F2.wireOp",EDGE,"E162");var subQ3=sQuery(id+"F2.wireOp",EDGE,"E160");var subQ5=makeQuery(id+"F2.imprint","INTERSECT",VERTEX,{"derivedFrom":[subQ3,subQ0]});Q72=makeQuery(id+"F2.imprint","IMPRINT",FACE,{"disambiguationData":[TD([[makeQuery(id+"F2.imprint","IMPRINT",EDGE,{"disambiguationData":[TD([[subQ5,1.0]])],"derivedFrom":subQ3}),1.0]])]});}
            var Q73;
            {var subQ0=sQuery(id+"F2.wireOp",EDGE,"E159");var subQ3=sQuery(id+"F2.wireOp",EDGE,"E164");var subQ4=makeQuery(id+"F2.imprint","INTERSECT",VERTEX,{"disambiguationData":[OD(0.0)],"derivedFrom":[subQ0,subQ3]});Q73=makeQuery(id+"F2.imprint","IMPRINT",FACE,{"disambiguationData":[TD([[makeQuery(id+"F2.imprint","IMPRINT",EDGE,{"disambiguationData":[TD([[subQ4,-1.0]])],"derivedFrom":subQ3}),-1.0]])]});}
            var Q74;
            {var subQ0=sQuery(id+"F2.wireOp",EDGE,"E156");Q74=makeQuery(id+"F2.imprint","IMPRINT",FACE,{"disambiguationData":[TD([[makeQuery(id+"F2.imprint","IMPRINT",EDGE,{"derivedFrom":subQ0}),-1.0]])]});}
            var Q75;
            {var subQ0=sQuery(id+"F2.wireOp",EDGE,"E159");var subQ3=sQuery(id+"F2.wireOp",EDGE,"E164");var subQ5=makeQuery(id+"F2.imprint","INTERSECT",VERTEX,{"disambiguationData":[OD(0.0)],"derivedFrom":[subQ0,subQ3]});Q75=makeQuery(id+"F2.imprint","IMPRINT",FACE,{"disambiguationData":[TD([[makeQuery(id+"F2.imprint","IMPRINT",EDGE,{"disambiguationData":[TD([[subQ5,1.0]])],"derivedFrom":subQ3}),-1.0]])]});}
            var Q76;
            {var subQ0=sQuery(id+"F2.wireOp",EDGE,"E162");var subQ3=sQuery(id+"F2.wireOp",EDGE,"E161");var subQ5=makeQuery(id+"F2.imprint","INTERSECT",VERTEX,{"derivedFrom":[subQ3,subQ0]});Q76=makeQuery(id+"F2.imprint","IMPRINT",FACE,{"disambiguationData":[TD([[makeQuery(id+"F2.imprint","IMPRINT",EDGE,{"disambiguationData":[TD([[subQ5,1.0]])],"derivedFrom":subQ3}),-1.0]])]});}
            var Q77;
            {var subQ0=sQuery(id+"F2.wireOp",EDGE,"E157");Q77=makeQuery(id+"F2.imprint","IMPRINT",FACE,{"disambiguationData":[TD([[makeQuery(id+"F2.imprint","IMPRINT",EDGE,{"derivedFrom":subQ0}),-1.0]])]});}
            var Q78;
            {var subQ0=sQuery(id+"F2.wireOp",EDGE,"E150");var subQ3=sQuery(id+"F2.wireOp",EDGE,"E148");var subQ5=makeQuery(id+"F2.imprint","INTERSECT",VERTEX,{"derivedFrom":[subQ3,subQ0]});Q78=makeQuery(id+"F2.imprint","IMPRINT",FACE,{"disambiguationData":[TD([[makeQuery(id+"F2.imprint","IMPRINT",EDGE,{"disambiguationData":[TD([[subQ5,1.0]])],"derivedFrom":subQ3}),1.0]])]});}
            var Q79;
            {var subQ0=sQuery(id+"F2.wireOp",EDGE,"E147");var subQ3=sQuery(id+"F2.wireOp",EDGE,"E152");var subQ4=makeQuery(id+"F2.imprint","INTERSECT",VERTEX,{"disambiguationData":[OD(0.0)],"derivedFrom":[subQ0,subQ3]});Q79=makeQuery(id+"F2.imprint","IMPRINT",FACE,{"disambiguationData":[TD([[makeQuery(id+"F2.imprint","IMPRINT",EDGE,{"disambiguationData":[TD([[subQ4,-1.0]])],"derivedFrom":subQ3}),-1.0]])]});}
            var Q80;
            {var subQ0=sQuery(id+"F2.wireOp",EDGE,"E144");Q80=makeQuery(id+"F2.imprint","IMPRINT",FACE,{"disambiguationData":[TD([[makeQuery(id+"F2.imprint","IMPRINT",EDGE,{"derivedFrom":subQ0}),-1.0]])]});}
            var Q81;
            {var subQ0=sQuery(id+"F2.wireOp",EDGE,"E147");var subQ3=sQuery(id+"F2.wireOp",EDGE,"E152");var subQ6=makeQuery(id+"F2.imprint","INTERSECT",VERTEX,{"disambiguationData":[OD(0.0)],"derivedFrom":[subQ0,subQ3]});Q81=makeQuery(id+"F2.imprint","IMPRINT",FACE,{"disambiguationData":[TD([[makeQuery(id+"F2.imprint","IMPRINT",EDGE,{"disambiguationData":[TD([[subQ6,1.0]])],"derivedFrom":subQ3}),-1.0]])]});}
            var Q82;
            {var subQ0=sQuery(id+"F2.wireOp",EDGE,"E145");Q82=makeQuery(id+"F2.imprint","IMPRINT",FACE,{"disambiguationData":[TD([[makeQuery(id+"F2.imprint","IMPRINT",EDGE,{"derivedFrom":subQ0}),-1.0]])]});}
            var Q83;
            {var subQ0=sQuery(id+"F2.wireOp",EDGE,"E150");var subQ3=sQuery(id+"F2.wireOp",EDGE,"E149");var subQ5=makeQuery(id+"F2.imprint","INTERSECT",VERTEX,{"derivedFrom":[subQ3,subQ0]});Q83=makeQuery(id+"F2.imprint","IMPRINT",FACE,{"disambiguationData":[TD([[makeQuery(id+"F2.imprint","IMPRINT",EDGE,{"disambiguationData":[TD([[subQ5,1.0]])],"derivedFrom":subQ3}),-1.0]])]});}
            var Q84;
            {var subQ0=sQuery(id+"F2.wireOp",EDGE,"E170");Q84=makeQuery(id+"F2.imprint","IMPRINT",FACE,{"disambiguationData":[TD([[makeQuery(id+"F2.imprint","IMPRINT",EDGE,{"derivedFrom":subQ0}),-1.0]])]});}
            var Q85;
            {var subQ0=sQuery(id+"F2.wireOp",EDGE,"E171");Q85=makeQuery(id+"F2.imprint","IMPRINT",FACE,{"disambiguationData":[TD([[makeQuery(id+"F2.imprint","IMPRINT",EDGE,{"derivedFrom":subQ0}),-1.0]])]});}
            var Q86;
            {var subQ0=sQuery(id+"F2.wireOp",EDGE,"E173");var subQ3=sQuery(id+"F2.wireOp",EDGE,"E178");var subQ6=makeQuery(id+"F2.imprint","INTERSECT",VERTEX,{"disambiguationData":[OD(0.0)],"derivedFrom":[subQ0,subQ3]});Q86=makeQuery(id+"F2.imprint","IMPRINT",FACE,{"disambiguationData":[TD([[makeQuery(id+"F2.imprint","IMPRINT",EDGE,{"disambiguationData":[TD([[subQ6,1.0]])],"derivedFrom":subQ3}),-1.0]])]});}
            var Q87;
            {var subQ0=sQuery(id+"F2.wireOp",EDGE,"E173");var subQ3=sQuery(id+"F2.wireOp",EDGE,"E178");var subQ4=makeQuery(id+"F2.imprint","INTERSECT",VERTEX,{"disambiguationData":[OD(0.0)],"derivedFrom":[subQ0,subQ3]});Q87=makeQuery(id+"F2.imprint","IMPRINT",FACE,{"disambiguationData":[TD([[makeQuery(id+"F2.imprint","IMPRINT",EDGE,{"disambiguationData":[TD([[subQ4,-1.0]])],"derivedFrom":subQ3}),-1.0]])]});}
            var Q88;
            {var subQ0=sQuery(id+"F2.wireOp",EDGE,"E176");var subQ3=sQuery(id+"F2.wireOp",EDGE,"E174");var subQ5=makeQuery(id+"F2.imprint","INTERSECT",VERTEX,{"derivedFrom":[subQ3,subQ0]});Q88=makeQuery(id+"F2.imprint","IMPRINT",FACE,{"disambiguationData":[TD([[makeQuery(id+"F2.imprint","IMPRINT",EDGE,{"disambiguationData":[TD([[subQ5,1.0]])],"derivedFrom":subQ3}),1.0]])]});}
            var Q89;
            {var subQ0=sQuery(id+"F2.wireOp",EDGE,"E176");var subQ3=sQuery(id+"F2.wireOp",EDGE,"E175");var subQ5=makeQuery(id+"F2.imprint","INTERSECT",VERTEX,{"derivedFrom":[subQ3,subQ0]});Q89=makeQuery(id+"F2.imprint","IMPRINT",FACE,{"disambiguationData":[TD([[makeQuery(id+"F2.imprint","IMPRINT",EDGE,{"disambiguationData":[TD([[subQ5,1.0]])],"derivedFrom":subQ3}),-1.0]])]});}
            var Q90;
            {var subQ10=sQuery(id+"F2.wireOp",EDGE,"E170");Q90=makeQuery(id+"F2.imprint","IMPRINT",FACE,{"disambiguationData":[TD([[makeQuery(id+"F2.imprint","IMPRINT",EDGE,{"derivedFrom":subQ10}),1.0]])]});}
            extrude(context, id + "F3", {"entities" : qUnion([Q0, Q1, Q2, Q3, Q4, Q5, Q6, Q7, Q8, Q9, Q10, Q11, Q12, Q13, Q14, Q15, Q16, Q17, Q18, Q19, Q20, Q21, Q22, Q23, Q24, Q25, Q26, Q27, Q28, Q29, Q30, Q31, Q32, Q33, Q34, Q35, Q36, Q37, Q38, Q39, Q40, Q41, Q42, Q43, Q44, Q45, Q46, Q47, Q48, Q49, Q50, Q51, Q52, Q53, Q54, Q55, Q56, Q57, Q58, Q59, Q60, Q61, Q62, Q63, Q64, Q65, Q66, Q67, Q68, Q69, Q70, Q71, Q72, Q73, Q74, Q75, Q76, Q77, Q78, Q79, Q80, Q81, Q82, Q83, Q84, Q85, Q86, Q87, Q88, Q89, Q90]), "operationType" : NewBodyOperationType.ADD, "oppositeDirection" : true, "depth" : 4 * mm, "offsetDistance" : 25 * mm});
        }
        {
            var Q0;
            {var subQ0=sQuery(id+"F2.wireOp",EDGE,"E22");Q0=makeQuery(id+"F2.imprint","IMPRINT",FACE,{"disambiguationData":[TD([[makeQuery(id+"F2.imprint","IMPRINT",EDGE,{"derivedFrom":subQ0}),1.0]])]});}
            var Q1;
            {var subQ0=sQuery(id+"F2.wireOp",EDGE,"E22");Q1=makeQuery(id+"F2.imprint","IMPRINT",FACE,{"disambiguationData":[TD([[makeQuery(id+"F2.imprint","IMPRINT",EDGE,{"derivedFrom":subQ0}),-1.0]])]});}
            var Q2;
            {var subQ0=sQuery(id+"F2.wireOp",EDGE,"E27");var subQ1=sQuery(id+"F2.wireOp",EDGE,"E22");var subQ2=makeQuery(id+"F2.imprint","INTERSECT",VERTEX,{"disambiguationData":[OD(0.0)],"derivedFrom":[subQ1,subQ0]});Q2=makeQuery(id+"F2.imprint","IMPRINT",FACE,{"disambiguationData":[TD([[makeQuery(id+"F2.imprint","IMPRINT",EDGE,{"disambiguationData":[TD([[subQ2,-1.0]])],"derivedFrom":subQ1}),-1.0]])]});}
            var Q3;
            {var subQ0=sQuery(id+"F2.wireOp",EDGE,"E27");var subQ1=sQuery(id+"F2.wireOp",EDGE,"E22");var subQ2=makeQuery(id+"F2.imprint","INTERSECT",VERTEX,{"disambiguationData":[OD(0.0)],"derivedFrom":[subQ1,subQ0]});Q3=makeQuery(id+"F2.imprint","IMPRINT",FACE,{"disambiguationData":[TD([[makeQuery(id+"F2.imprint","IMPRINT",EDGE,{"disambiguationData":[TD([[subQ2,-1.0]])],"derivedFrom":subQ1}),1.0]])]});}
            var Q4;
            {var subQ0=sQuery(id+"F2.wireOp",EDGE,"E33");var subQ3=sQuery(id+"F2.wireOp",EDGE,"E38");var subQ4=makeQuery(id+"F2.imprint","INTERSECT",VERTEX,{"disambiguationData":[OD(0.0)],"derivedFrom":[subQ0,subQ3]});Q4=makeQuery(id+"F2.imprint","IMPRINT",FACE,{"disambiguationData":[TD([[makeQuery(id+"F2.imprint","IMPRINT",EDGE,{"disambiguationData":[TD([[subQ4,-1.0]])],"derivedFrom":subQ3}),-1.0]])]});}
            var Q5;
            {var subQ0=sQuery(id+"F2.wireOp",EDGE,"E33");var subQ3=sQuery(id+"F2.wireOp",EDGE,"E38");var subQ6=makeQuery(id+"F2.imprint","INTERSECT",VERTEX,{"disambiguationData":[OD(0.0)],"derivedFrom":[subQ0,subQ3]});Q5=makeQuery(id+"F2.imprint","IMPRINT",FACE,{"disambiguationData":[TD([[makeQuery(id+"F2.imprint","IMPRINT",EDGE,{"disambiguationData":[TD([[subQ6,1.0]])],"derivedFrom":subQ3}),-1.0]])]});}
            var Q6;
            {var subQ0=sQuery(id+"F2.wireOp",EDGE,"E38");var subQ1=sQuery(id+"F2.wireOp",EDGE,"E33");var subQ2=makeQuery(id+"F2.imprint","INTERSECT",VERTEX,{"disambiguationData":[OD(0.0)],"derivedFrom":[subQ1,subQ0]});Q6=makeQuery(id+"F2.imprint","IMPRINT",FACE,{"disambiguationData":[TD([[makeQuery(id+"F2.imprint","IMPRINT",EDGE,{"disambiguationData":[TD([[subQ2,-1.0]])],"derivedFrom":subQ1}),-1.0]])]});}
            var Q7;
            {var subQ0=sQuery(id+"F2.wireOp",EDGE,"E38");var subQ1=sQuery(id+"F2.wireOp",EDGE,"E33");var subQ2=makeQuery(id+"F2.imprint","INTERSECT",VERTEX,{"disambiguationData":[OD(0.0)],"derivedFrom":[subQ1,subQ0]});Q7=makeQuery(id+"F2.imprint","IMPRINT",FACE,{"disambiguationData":[TD([[makeQuery(id+"F2.imprint","IMPRINT",EDGE,{"disambiguationData":[TD([[subQ2,-1.0]])],"derivedFrom":subQ1}),1.0]])]});}
            var Q8;
            {var subQ0=sQuery(id+"F2.wireOp",EDGE,"E47");var subQ3=sQuery(id+"F2.wireOp",EDGE,"E52");var subQ6=makeQuery(id+"F2.imprint","INTERSECT",VERTEX,{"disambiguationData":[OD(0.0)],"derivedFrom":[subQ0,subQ3]});Q8=makeQuery(id+"F2.imprint","IMPRINT",FACE,{"disambiguationData":[TD([[makeQuery(id+"F2.imprint","IMPRINT",EDGE,{"disambiguationData":[TD([[subQ6,1.0]])],"derivedFrom":subQ3}),-1.0]])]});}
            var Q9;
            {var subQ0=sQuery(id+"F2.wireOp",EDGE,"E47");var subQ3=sQuery(id+"F2.wireOp",EDGE,"E52");var subQ4=makeQuery(id+"F2.imprint","INTERSECT",VERTEX,{"disambiguationData":[OD(0.0)],"derivedFrom":[subQ0,subQ3]});Q9=makeQuery(id+"F2.imprint","IMPRINT",FACE,{"disambiguationData":[TD([[makeQuery(id+"F2.imprint","IMPRINT",EDGE,{"disambiguationData":[TD([[subQ4,-1.0]])],"derivedFrom":subQ3}),-1.0]])]});}
            var Q10;
            {var subQ0=sQuery(id+"F2.wireOp",EDGE,"E52");var subQ1=sQuery(id+"F2.wireOp",EDGE,"E47");var subQ2=makeQuery(id+"F2.imprint","INTERSECT",VERTEX,{"disambiguationData":[OD(0.0)],"derivedFrom":[subQ1,subQ0]});Q10=makeQuery(id+"F2.imprint","IMPRINT",FACE,{"disambiguationData":[TD([[makeQuery(id+"F2.imprint","IMPRINT",EDGE,{"disambiguationData":[TD([[subQ2,-1.0]])],"derivedFrom":subQ1}),1.0]])]});}
            var Q11;
            {var subQ0=sQuery(id+"F2.wireOp",EDGE,"E52");var subQ1=sQuery(id+"F2.wireOp",EDGE,"E47");var subQ2=makeQuery(id+"F2.imprint","INTERSECT",VERTEX,{"disambiguationData":[OD(0.0)],"derivedFrom":[subQ1,subQ0]});Q11=makeQuery(id+"F2.imprint","IMPRINT",FACE,{"disambiguationData":[TD([[makeQuery(id+"F2.imprint","IMPRINT",EDGE,{"disambiguationData":[TD([[subQ2,-1.0]])],"derivedFrom":subQ1}),-1.0]])]});}
            var Q12;
            {var subQ0=sQuery(id+"F2.wireOp",EDGE,"E60");var subQ3=sQuery(id+"F2.wireOp",EDGE,"E65");var subQ6=makeQuery(id+"F2.imprint","INTERSECT",VERTEX,{"disambiguationData":[OD(0.0)],"derivedFrom":[subQ0,subQ3]});Q12=makeQuery(id+"F2.imprint","IMPRINT",FACE,{"disambiguationData":[TD([[makeQuery(id+"F2.imprint","IMPRINT",EDGE,{"disambiguationData":[TD([[subQ6,1.0]])],"derivedFrom":subQ3}),-1.0]])]});}
            var Q13;
            {var subQ0=sQuery(id+"F2.wireOp",EDGE,"E60");var subQ3=sQuery(id+"F2.wireOp",EDGE,"E65");var subQ4=makeQuery(id+"F2.imprint","INTERSECT",VERTEX,{"disambiguationData":[OD(0.0)],"derivedFrom":[subQ0,subQ3]});Q13=makeQuery(id+"F2.imprint","IMPRINT",FACE,{"disambiguationData":[TD([[makeQuery(id+"F2.imprint","IMPRINT",EDGE,{"disambiguationData":[TD([[subQ4,-1.0]])],"derivedFrom":subQ3}),-1.0]])]});}
            var Q14;
            {var subQ0=sQuery(id+"F2.wireOp",EDGE,"E65");var subQ1=sQuery(id+"F2.wireOp",EDGE,"E60");var subQ2=makeQuery(id+"F2.imprint","INTERSECT",VERTEX,{"disambiguationData":[OD(0.0)],"derivedFrom":[subQ1,subQ0]});Q14=makeQuery(id+"F2.imprint","IMPRINT",FACE,{"disambiguationData":[TD([[makeQuery(id+"F2.imprint","IMPRINT",EDGE,{"disambiguationData":[TD([[subQ2,-1.0]])],"derivedFrom":subQ1}),-1.0]])]});}
            var Q15;
            {var subQ0=sQuery(id+"F2.wireOp",EDGE,"E65");var subQ1=sQuery(id+"F2.wireOp",EDGE,"E60");var subQ2=makeQuery(id+"F2.imprint","INTERSECT",VERTEX,{"disambiguationData":[OD(0.0)],"derivedFrom":[subQ1,subQ0]});Q15=makeQuery(id+"F2.imprint","IMPRINT",FACE,{"disambiguationData":[TD([[makeQuery(id+"F2.imprint","IMPRINT",EDGE,{"disambiguationData":[TD([[subQ2,-1.0]])],"derivedFrom":subQ1}),1.0]])]});}
            var Q16;
            {var subQ0=sQuery(id+"F2.wireOp",EDGE,"E74");var subQ3=sQuery(id+"F2.wireOp",EDGE,"E79");var subQ6=makeQuery(id+"F2.imprint","INTERSECT",VERTEX,{"disambiguationData":[OD(0.0)],"derivedFrom":[subQ0,subQ3]});Q16=makeQuery(id+"F2.imprint","IMPRINT",FACE,{"disambiguationData":[TD([[makeQuery(id+"F2.imprint","IMPRINT",EDGE,{"disambiguationData":[TD([[subQ6,1.0]])],"derivedFrom":subQ3}),-1.0]])]});}
            var Q17;
            {var subQ0=sQuery(id+"F2.wireOp",EDGE,"E79");var subQ1=sQuery(id+"F2.wireOp",EDGE,"E74");var subQ2=makeQuery(id+"F2.imprint","INTERSECT",VERTEX,{"disambiguationData":[OD(0.0)],"derivedFrom":[subQ1,subQ0]});Q17=makeQuery(id+"F2.imprint","IMPRINT",FACE,{"disambiguationData":[TD([[makeQuery(id+"F2.imprint","IMPRINT",EDGE,{"disambiguationData":[TD([[subQ2,-1.0]])],"derivedFrom":subQ1}),1.0]])]});}
            var Q18;
            {var subQ0=sQuery(id+"F2.wireOp",EDGE,"E79");var subQ1=sQuery(id+"F2.wireOp",EDGE,"E74");var subQ2=makeQuery(id+"F2.imprint","INTERSECT",VERTEX,{"disambiguationData":[OD(0.0)],"derivedFrom":[subQ1,subQ0]});Q18=makeQuery(id+"F2.imprint","IMPRINT",FACE,{"disambiguationData":[TD([[makeQuery(id+"F2.imprint","IMPRINT",EDGE,{"disambiguationData":[TD([[subQ2,-1.0]])],"derivedFrom":subQ1}),-1.0]])]});}
            var Q19;
            {var subQ0=sQuery(id+"F2.wireOp",EDGE,"E74");var subQ3=sQuery(id+"F2.wireOp",EDGE,"E79");var subQ4=makeQuery(id+"F2.imprint","INTERSECT",VERTEX,{"disambiguationData":[OD(0.0)],"derivedFrom":[subQ0,subQ3]});Q19=makeQuery(id+"F2.imprint","IMPRINT",FACE,{"disambiguationData":[TD([[makeQuery(id+"F2.imprint","IMPRINT",EDGE,{"disambiguationData":[TD([[subQ4,-1.0]])],"derivedFrom":subQ3}),-1.0]])]});}
            var Q20;
            {var subQ0=sQuery(id+"F2.wireOp",EDGE,"E86");var subQ3=sQuery(id+"F2.wireOp",EDGE,"E91");var subQ6=makeQuery(id+"F2.imprint","INTERSECT",VERTEX,{"disambiguationData":[OD(0.0)],"derivedFrom":[subQ0,subQ3]});Q20=makeQuery(id+"F2.imprint","IMPRINT",FACE,{"disambiguationData":[TD([[makeQuery(id+"F2.imprint","IMPRINT",EDGE,{"disambiguationData":[TD([[subQ6,1.0]])],"derivedFrom":subQ3}),-1.0]])]});}
            var Q21;
            {var subQ0=sQuery(id+"F2.wireOp",EDGE,"E86");var subQ3=sQuery(id+"F2.wireOp",EDGE,"E91");var subQ4=makeQuery(id+"F2.imprint","INTERSECT",VERTEX,{"disambiguationData":[OD(0.0)],"derivedFrom":[subQ0,subQ3]});Q21=makeQuery(id+"F2.imprint","IMPRINT",FACE,{"disambiguationData":[TD([[makeQuery(id+"F2.imprint","IMPRINT",EDGE,{"disambiguationData":[TD([[subQ4,-1.0]])],"derivedFrom":subQ3}),-1.0]])]});}
            var Q22;
            {var subQ0=sQuery(id+"F2.wireOp",EDGE,"E91");var subQ1=sQuery(id+"F2.wireOp",EDGE,"E86");var subQ2=makeQuery(id+"F2.imprint","INTERSECT",VERTEX,{"disambiguationData":[OD(0.0)],"derivedFrom":[subQ1,subQ0]});Q22=makeQuery(id+"F2.imprint","IMPRINT",FACE,{"disambiguationData":[TD([[makeQuery(id+"F2.imprint","IMPRINT",EDGE,{"disambiguationData":[TD([[subQ2,-1.0]])],"derivedFrom":subQ1}),1.0]])]});}
            var Q23;
            {var subQ0=sQuery(id+"F2.wireOp",EDGE,"E91");var subQ1=sQuery(id+"F2.wireOp",EDGE,"E86");var subQ2=makeQuery(id+"F2.imprint","INTERSECT",VERTEX,{"disambiguationData":[OD(0.0)],"derivedFrom":[subQ1,subQ0]});Q23=makeQuery(id+"F2.imprint","IMPRINT",FACE,{"disambiguationData":[TD([[makeQuery(id+"F2.imprint","IMPRINT",EDGE,{"disambiguationData":[TD([[subQ2,-1.0]])],"derivedFrom":subQ1}),-1.0]])]});}
            var Q24;
            {var subQ0=sQuery(id+"F2.wireOp",EDGE,"E98");var subQ3=sQuery(id+"F2.wireOp",EDGE,"E103");var subQ4=makeQuery(id+"F2.imprint","INTERSECT",VERTEX,{"disambiguationData":[OD(0.0)],"derivedFrom":[subQ0,subQ3]});Q24=makeQuery(id+"F2.imprint","IMPRINT",FACE,{"disambiguationData":[TD([[makeQuery(id+"F2.imprint","IMPRINT",EDGE,{"disambiguationData":[TD([[subQ4,-1.0]])],"derivedFrom":subQ3}),-1.0]])]});}
            var Q25;
            {var subQ0=sQuery(id+"F2.wireOp",EDGE,"E98");var subQ3=sQuery(id+"F2.wireOp",EDGE,"E103");var subQ6=makeQuery(id+"F2.imprint","INTERSECT",VERTEX,{"disambiguationData":[OD(0.0)],"derivedFrom":[subQ0,subQ3]});Q25=makeQuery(id+"F2.imprint","IMPRINT",FACE,{"disambiguationData":[TD([[makeQuery(id+"F2.imprint","IMPRINT",EDGE,{"disambiguationData":[TD([[subQ6,1.0]])],"derivedFrom":subQ3}),-1.0]])]});}
            var Q26;
            {var subQ0=sQuery(id+"F2.wireOp",EDGE,"E103");var subQ1=sQuery(id+"F2.wireOp",EDGE,"E98");var subQ2=makeQuery(id+"F2.imprint","INTERSECT",VERTEX,{"disambiguationData":[OD(0.0)],"derivedFrom":[subQ1,subQ0]});Q26=makeQuery(id+"F2.imprint","IMPRINT",FACE,{"disambiguationData":[TD([[makeQuery(id+"F2.imprint","IMPRINT",EDGE,{"disambiguationData":[TD([[subQ2,-1.0]])],"derivedFrom":subQ1}),-1.0]])]});}
            var Q27;
            {var subQ0=sQuery(id+"F2.wireOp",EDGE,"E103");var subQ1=sQuery(id+"F2.wireOp",EDGE,"E98");var subQ2=makeQuery(id+"F2.imprint","INTERSECT",VERTEX,{"disambiguationData":[OD(0.0)],"derivedFrom":[subQ1,subQ0]});Q27=makeQuery(id+"F2.imprint","IMPRINT",FACE,{"disambiguationData":[TD([[makeQuery(id+"F2.imprint","IMPRINT",EDGE,{"disambiguationData":[TD([[subQ2,-1.0]])],"derivedFrom":subQ1}),1.0]])]});}
            var Q28;
            {var subQ0=sQuery(id+"F2.wireOp",EDGE,"E110");var subQ3=sQuery(id+"F2.wireOp",EDGE,"E115");var subQ6=makeQuery(id+"F2.imprint","INTERSECT",VERTEX,{"disambiguationData":[OD(0.0)],"derivedFrom":[subQ0,subQ3]});Q28=makeQuery(id+"F2.imprint","IMPRINT",FACE,{"disambiguationData":[TD([[makeQuery(id+"F2.imprint","IMPRINT",EDGE,{"disambiguationData":[TD([[subQ6,1.0]])],"derivedFrom":subQ3}),-1.0]])]});}
            var Q29;
            {var subQ0=sQuery(id+"F2.wireOp",EDGE,"E110");var subQ3=sQuery(id+"F2.wireOp",EDGE,"E115");var subQ4=makeQuery(id+"F2.imprint","INTERSECT",VERTEX,{"disambiguationData":[OD(0.0)],"derivedFrom":[subQ0,subQ3]});Q29=makeQuery(id+"F2.imprint","IMPRINT",FACE,{"disambiguationData":[TD([[makeQuery(id+"F2.imprint","IMPRINT",EDGE,{"disambiguationData":[TD([[subQ4,-1.0]])],"derivedFrom":subQ3}),-1.0]])]});}
            var Q30;
            {var subQ0=sQuery(id+"F2.wireOp",EDGE,"E115");var subQ1=sQuery(id+"F2.wireOp",EDGE,"E110");var subQ2=makeQuery(id+"F2.imprint","INTERSECT",VERTEX,{"disambiguationData":[OD(0.0)],"derivedFrom":[subQ1,subQ0]});Q30=makeQuery(id+"F2.imprint","IMPRINT",FACE,{"disambiguationData":[TD([[makeQuery(id+"F2.imprint","IMPRINT",EDGE,{"disambiguationData":[TD([[subQ2,-1.0]])],"derivedFrom":subQ1}),1.0]])]});}
            var Q31;
            {var subQ0=sQuery(id+"F2.wireOp",EDGE,"E115");var subQ1=sQuery(id+"F2.wireOp",EDGE,"E110");var subQ2=makeQuery(id+"F2.imprint","INTERSECT",VERTEX,{"disambiguationData":[OD(0.0)],"derivedFrom":[subQ1,subQ0]});Q31=makeQuery(id+"F2.imprint","IMPRINT",FACE,{"disambiguationData":[TD([[makeQuery(id+"F2.imprint","IMPRINT",EDGE,{"disambiguationData":[TD([[subQ2,-1.0]])],"derivedFrom":subQ1}),-1.0]])]});}
            var Q32;
            {var subQ0=sQuery(id+"F2.wireOp",EDGE,"E122");var subQ3=sQuery(id+"F2.wireOp",EDGE,"E127");var subQ4=makeQuery(id+"F2.imprint","INTERSECT",VERTEX,{"disambiguationData":[OD(0.0)],"derivedFrom":[subQ0,subQ3]});Q32=makeQuery(id+"F2.imprint","IMPRINT",FACE,{"disambiguationData":[TD([[makeQuery(id+"F2.imprint","IMPRINT",EDGE,{"disambiguationData":[TD([[subQ4,-1.0]])],"derivedFrom":subQ3}),-1.0]])]});}
            var Q33;
            {var subQ0=sQuery(id+"F2.wireOp",EDGE,"E127");var subQ1=sQuery(id+"F2.wireOp",EDGE,"E122");var subQ2=makeQuery(id+"F2.imprint","INTERSECT",VERTEX,{"disambiguationData":[OD(0.0)],"derivedFrom":[subQ1,subQ0]});Q33=makeQuery(id+"F2.imprint","IMPRINT",FACE,{"disambiguationData":[TD([[makeQuery(id+"F2.imprint","IMPRINT",EDGE,{"disambiguationData":[TD([[subQ2,-1.0]])],"derivedFrom":subQ1}),-1.0]])]});}
            var Q34;
            {var subQ0=sQuery(id+"F2.wireOp",EDGE,"E127");var subQ1=sQuery(id+"F2.wireOp",EDGE,"E122");var subQ2=makeQuery(id+"F2.imprint","INTERSECT",VERTEX,{"disambiguationData":[OD(0.0)],"derivedFrom":[subQ1,subQ0]});Q34=makeQuery(id+"F2.imprint","IMPRINT",FACE,{"disambiguationData":[TD([[makeQuery(id+"F2.imprint","IMPRINT",EDGE,{"disambiguationData":[TD([[subQ2,-1.0]])],"derivedFrom":subQ1}),1.0]])]});}
            var Q35;
            {var subQ0=sQuery(id+"F2.wireOp",EDGE,"E122");var subQ3=sQuery(id+"F2.wireOp",EDGE,"E127");var subQ6=makeQuery(id+"F2.imprint","INTERSECT",VERTEX,{"disambiguationData":[OD(0.0)],"derivedFrom":[subQ0,subQ3]});Q35=makeQuery(id+"F2.imprint","IMPRINT",FACE,{"disambiguationData":[TD([[makeQuery(id+"F2.imprint","IMPRINT",EDGE,{"disambiguationData":[TD([[subQ6,1.0]])],"derivedFrom":subQ3}),-1.0]])]});}
            var Q36;
            {var subQ0=sQuery(id+"F2.wireOp",EDGE,"E134");var subQ3=sQuery(id+"F2.wireOp",EDGE,"E139");var subQ4=makeQuery(id+"F2.imprint","INTERSECT",VERTEX,{"disambiguationData":[OD(0.0)],"derivedFrom":[subQ0,subQ3]});Q36=makeQuery(id+"F2.imprint","IMPRINT",FACE,{"disambiguationData":[TD([[makeQuery(id+"F2.imprint","IMPRINT",EDGE,{"disambiguationData":[TD([[subQ4,-1.0]])],"derivedFrom":subQ3}),-1.0]])]});}
            var Q37;
            {var subQ0=sQuery(id+"F2.wireOp",EDGE,"E139");var subQ1=sQuery(id+"F2.wireOp",EDGE,"E134");var subQ2=makeQuery(id+"F2.imprint","INTERSECT",VERTEX,{"disambiguationData":[OD(0.0)],"derivedFrom":[subQ1,subQ0]});Q37=makeQuery(id+"F2.imprint","IMPRINT",FACE,{"disambiguationData":[TD([[makeQuery(id+"F2.imprint","IMPRINT",EDGE,{"disambiguationData":[TD([[subQ2,-1.0]])],"derivedFrom":subQ1}),-1.0]])]});}
            var Q38;
            {var subQ0=sQuery(id+"F2.wireOp",EDGE,"E139");var subQ1=sQuery(id+"F2.wireOp",EDGE,"E134");var subQ2=makeQuery(id+"F2.imprint","INTERSECT",VERTEX,{"disambiguationData":[OD(0.0)],"derivedFrom":[subQ1,subQ0]});Q38=makeQuery(id+"F2.imprint","IMPRINT",FACE,{"disambiguationData":[TD([[makeQuery(id+"F2.imprint","IMPRINT",EDGE,{"disambiguationData":[TD([[subQ2,-1.0]])],"derivedFrom":subQ1}),1.0]])]});}
            var Q39;
            {var subQ0=sQuery(id+"F2.wireOp",EDGE,"E134");var subQ3=sQuery(id+"F2.wireOp",EDGE,"E139");var subQ6=makeQuery(id+"F2.imprint","INTERSECT",VERTEX,{"disambiguationData":[OD(0.0)],"derivedFrom":[subQ0,subQ3]});Q39=makeQuery(id+"F2.imprint","IMPRINT",FACE,{"disambiguationData":[TD([[makeQuery(id+"F2.imprint","IMPRINT",EDGE,{"disambiguationData":[TD([[subQ6,1.0]])],"derivedFrom":subQ3}),-1.0]])]});}
            var Q40;
            {var subQ0=sQuery(id+"F2.wireOp",EDGE,"E147");var subQ3=sQuery(id+"F2.wireOp",EDGE,"E152");var subQ4=makeQuery(id+"F2.imprint","INTERSECT",VERTEX,{"disambiguationData":[OD(0.0)],"derivedFrom":[subQ0,subQ3]});Q40=makeQuery(id+"F2.imprint","IMPRINT",FACE,{"disambiguationData":[TD([[makeQuery(id+"F2.imprint","IMPRINT",EDGE,{"disambiguationData":[TD([[subQ4,-1.0]])],"derivedFrom":subQ3}),-1.0]])]});}
            var Q41;
            {var subQ0=sQuery(id+"F2.wireOp",EDGE,"E147");var subQ3=sQuery(id+"F2.wireOp",EDGE,"E152");var subQ6=makeQuery(id+"F2.imprint","INTERSECT",VERTEX,{"disambiguationData":[OD(0.0)],"derivedFrom":[subQ0,subQ3]});Q41=makeQuery(id+"F2.imprint","IMPRINT",FACE,{"disambiguationData":[TD([[makeQuery(id+"F2.imprint","IMPRINT",EDGE,{"disambiguationData":[TD([[subQ6,1.0]])],"derivedFrom":subQ3}),-1.0]])]});}
            var Q42;
            {var subQ0=sQuery(id+"F2.wireOp",EDGE,"E152");var subQ1=sQuery(id+"F2.wireOp",EDGE,"E147");var subQ2=makeQuery(id+"F2.imprint","INTERSECT",VERTEX,{"disambiguationData":[OD(0.0)],"derivedFrom":[subQ1,subQ0]});Q42=makeQuery(id+"F2.imprint","IMPRINT",FACE,{"disambiguationData":[TD([[makeQuery(id+"F2.imprint","IMPRINT",EDGE,{"disambiguationData":[TD([[subQ2,-1.0]])],"derivedFrom":subQ1}),-1.0]])]});}
            var Q43;
            {var subQ0=sQuery(id+"F2.wireOp",EDGE,"E152");var subQ1=sQuery(id+"F2.wireOp",EDGE,"E147");var subQ2=makeQuery(id+"F2.imprint","INTERSECT",VERTEX,{"disambiguationData":[OD(0.0)],"derivedFrom":[subQ1,subQ0]});Q43=makeQuery(id+"F2.imprint","IMPRINT",FACE,{"disambiguationData":[TD([[makeQuery(id+"F2.imprint","IMPRINT",EDGE,{"disambiguationData":[TD([[subQ2,-1.0]])],"derivedFrom":subQ1}),1.0]])]});}
            var Q44;
            {var subQ0=sQuery(id+"F2.wireOp",EDGE,"E159");var subQ3=sQuery(id+"F2.wireOp",EDGE,"E164");var subQ4=makeQuery(id+"F2.imprint","INTERSECT",VERTEX,{"disambiguationData":[OD(0.0)],"derivedFrom":[subQ0,subQ3]});Q44=makeQuery(id+"F2.imprint","IMPRINT",FACE,{"disambiguationData":[TD([[makeQuery(id+"F2.imprint","IMPRINT",EDGE,{"disambiguationData":[TD([[subQ4,-1.0]])],"derivedFrom":subQ3}),-1.0]])]});}
            var Q45;
            {var subQ0=sQuery(id+"F2.wireOp",EDGE,"E164");var subQ1=sQuery(id+"F2.wireOp",EDGE,"E159");var subQ2=makeQuery(id+"F2.imprint","INTERSECT",VERTEX,{"disambiguationData":[OD(0.0)],"derivedFrom":[subQ1,subQ0]});Q45=makeQuery(id+"F2.imprint","IMPRINT",FACE,{"disambiguationData":[TD([[makeQuery(id+"F2.imprint","IMPRINT",EDGE,{"disambiguationData":[TD([[subQ2,-1.0]])],"derivedFrom":subQ1}),-1.0]])]});}
            var Q46;
            {var subQ0=sQuery(id+"F2.wireOp",EDGE,"E159");var subQ3=sQuery(id+"F2.wireOp",EDGE,"E164");var subQ5=makeQuery(id+"F2.imprint","INTERSECT",VERTEX,{"disambiguationData":[OD(0.0)],"derivedFrom":[subQ0,subQ3]});Q46=makeQuery(id+"F2.imprint","IMPRINT",FACE,{"disambiguationData":[TD([[makeQuery(id+"F2.imprint","IMPRINT",EDGE,{"disambiguationData":[TD([[subQ5,1.0]])],"derivedFrom":subQ3}),-1.0]])]});}
            var Q47;
            {var subQ0=sQuery(id+"F2.wireOp",EDGE,"E164");var subQ1=sQuery(id+"F2.wireOp",EDGE,"E159");var subQ2=makeQuery(id+"F2.imprint","INTERSECT",VERTEX,{"disambiguationData":[OD(0.0)],"derivedFrom":[subQ1,subQ0]});Q47=makeQuery(id+"F2.imprint","IMPRINT",FACE,{"disambiguationData":[TD([[makeQuery(id+"F2.imprint","IMPRINT",EDGE,{"disambiguationData":[TD([[subQ2,-1.0]])],"derivedFrom":subQ1}),1.0]])]});}
            var Q48;
            {var subQ0=sQuery(id+"F2.wireOp",EDGE,"E173");var subQ3=sQuery(id+"F2.wireOp",EDGE,"E178");var subQ4=makeQuery(id+"F2.imprint","INTERSECT",VERTEX,{"disambiguationData":[OD(0.0)],"derivedFrom":[subQ0,subQ3]});Q48=makeQuery(id+"F2.imprint","IMPRINT",FACE,{"disambiguationData":[TD([[makeQuery(id+"F2.imprint","IMPRINT",EDGE,{"disambiguationData":[TD([[subQ4,-1.0]])],"derivedFrom":subQ3}),-1.0]])]});}
            var Q49;
            {var subQ0=sQuery(id+"F2.wireOp",EDGE,"E178");var subQ1=sQuery(id+"F2.wireOp",EDGE,"E173");var subQ2=makeQuery(id+"F2.imprint","INTERSECT",VERTEX,{"disambiguationData":[OD(0.0)],"derivedFrom":[subQ1,subQ0]});Q49=makeQuery(id+"F2.imprint","IMPRINT",FACE,{"disambiguationData":[TD([[makeQuery(id+"F2.imprint","IMPRINT",EDGE,{"disambiguationData":[TD([[subQ2,-1.0]])],"derivedFrom":subQ1}),-1.0]])]});}
            var Q50;
            {var subQ0=sQuery(id+"F2.wireOp",EDGE,"E173");var subQ3=sQuery(id+"F2.wireOp",EDGE,"E178");var subQ6=makeQuery(id+"F2.imprint","INTERSECT",VERTEX,{"disambiguationData":[OD(0.0)],"derivedFrom":[subQ0,subQ3]});Q50=makeQuery(id+"F2.imprint","IMPRINT",FACE,{"disambiguationData":[TD([[makeQuery(id+"F2.imprint","IMPRINT",EDGE,{"disambiguationData":[TD([[subQ6,1.0]])],"derivedFrom":subQ3}),-1.0]])]});}
            var Q51;
            {var subQ0=sQuery(id+"F2.wireOp",EDGE,"E178");var subQ1=sQuery(id+"F2.wireOp",EDGE,"E173");var subQ2=makeQuery(id+"F2.imprint","INTERSECT",VERTEX,{"disambiguationData":[OD(0.0)],"derivedFrom":[subQ1,subQ0]});Q51=makeQuery(id+"F2.imprint","IMPRINT",FACE,{"disambiguationData":[TD([[makeQuery(id+"F2.imprint","IMPRINT",EDGE,{"disambiguationData":[TD([[subQ2,-1.0]])],"derivedFrom":subQ1}),1.0]])]});}
            var Q52;
            Q52=makeQuery(id+"F1.opExtrude","CAP_FACE",FACE,{"disambiguationData":[OSD([sQuery(id+"F0.wireOp",EDGE,"E0"),sQuery(id+"F0.wireOp",EDGE,"E1"),sQuery(id+"F0.wireOp",EDGE,"E2"),sQuery(id+"F0.wireOp",EDGE,"E3"),sQuery(id+"F0.wireOp",EDGE,"E4"),sQuery(id+"F0.wireOp",EDGE,"E5"),sQuery(id+"F0.wireOp",EDGE,"E6"),sQuery(id+"F0.wireOp",EDGE,"E7"),sQuery(id+"F0.wireOp",EDGE,"E8"),sQuery(id+"F0.wireOp",EDGE,"E9"),sQuery(id+"F0.wireOp",EDGE,"E10")])],"isStart":false});
            extrude(context, id + "F4", {"entities" : qUnion([Q0, Q1, Q2, Q3, Q4, Q5, Q6, Q7, Q8, Q9, Q10, Q11, Q12, Q13, Q14, Q15, Q16, Q17, Q18, Q19, Q20, Q21, Q22, Q23, Q24, Q25, Q26, Q27, Q28, Q29, Q30, Q31, Q32, Q33, Q34, Q35, Q36, Q37, Q38, Q39, Q40, Q41, Q42, Q43, Q44, Q45, Q46, Q47, Q48, Q49, Q50, Q51]), "operationType" : NewBodyOperationType.REMOVE, "oppositeDirection" : true, "depth" : 3 * mm, "endBoundEntityFace" : qUnion([Q52]), "offsetDistance" : 25 * mm});
        }
        {
            var Q0;
            Q0=makeQuery(id+"F1.opExtrude","SWEPT_BODY",BODY,{"disambiguationData":[OSD([sQuery(id+"F0.wireOp",EDGE,"E0"),sQuery(id+"F0.wireOp",EDGE,"E1"),sQuery(id+"F0.wireOp",EDGE,"E2"),sQuery(id+"F0.wireOp",EDGE,"E3"),sQuery(id+"F0.wireOp",EDGE,"E4"),sQuery(id+"F0.wireOp",EDGE,"E5"),sQuery(id+"F0.wireOp",EDGE,"E6"),sQuery(id+"F0.wireOp",EDGE,"E7"),sQuery(id+"F0.wireOp",EDGE,"E8"),sQuery(id+"F0.wireOp",EDGE,"E9"),sQuery(id+"F0.wireOp",EDGE,"E10")])]});
            var Q1;
            Q1=qCreatedBy(makeId("Right.planeOp"),FACE);
            mirror(context, id + "F5", {"entities" : qUnion([Q0]), "mirrorPlane" : qUnion([Q1])});
        }
    });
